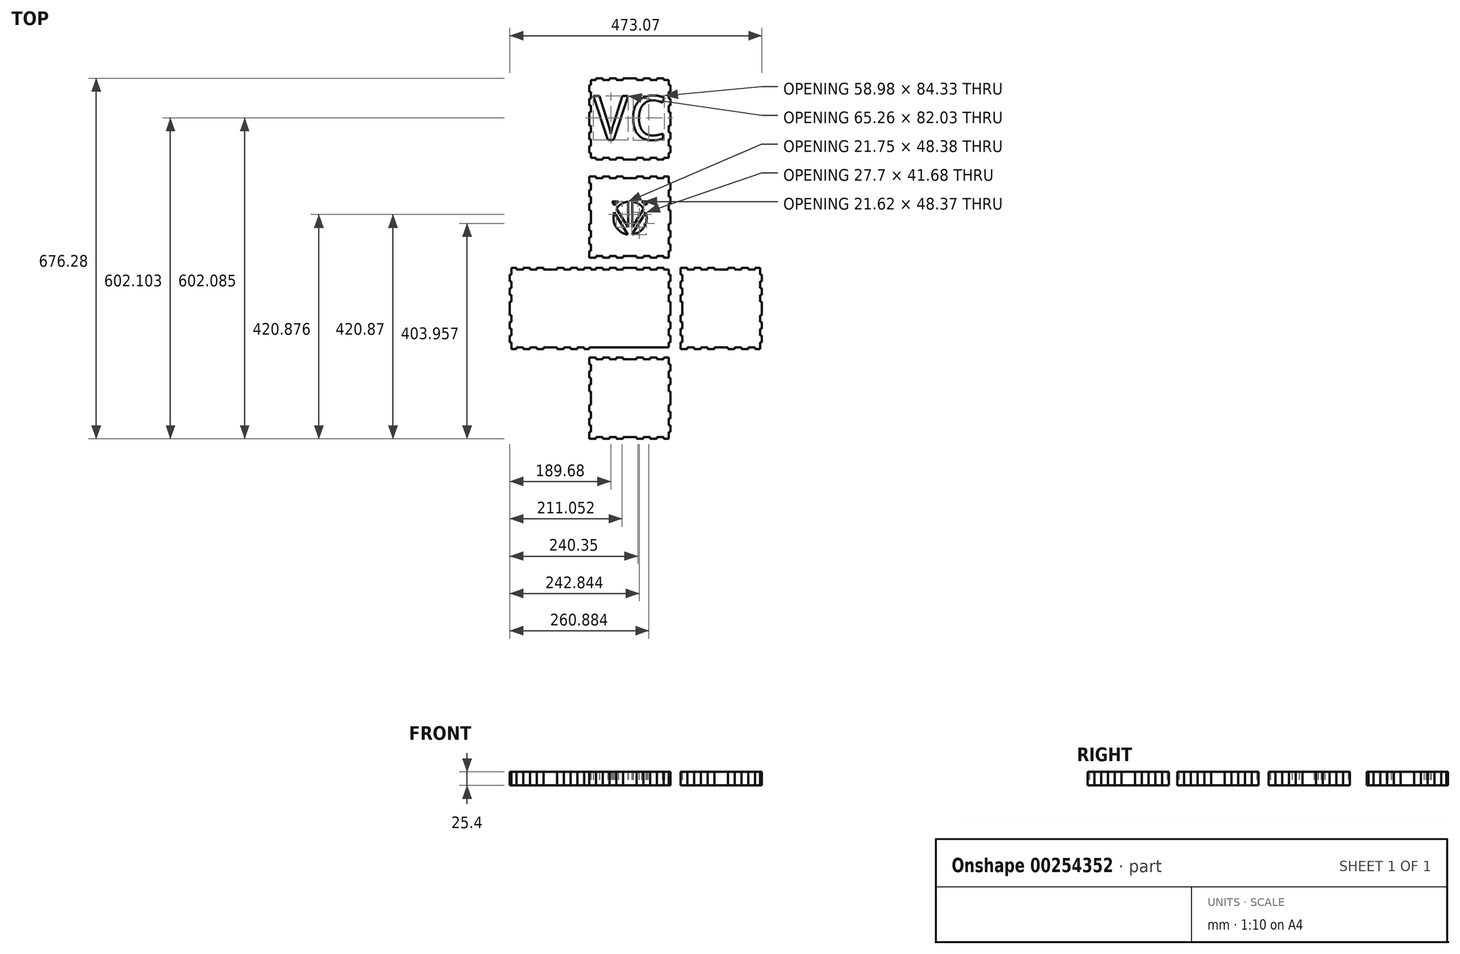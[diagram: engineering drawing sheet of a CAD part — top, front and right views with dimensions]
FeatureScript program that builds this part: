
annotation { "Feature Type Name" : "Feature", "Feature Type Description" : "" }
export const myFeature = defineFeature(function(context is Context, id is Id, definition is map)
    precondition{}
    {
        {
            var Q0;
            Q0=qCreatedBy(makeId("Top.planeOp"),FACE);
            var sketch = newSketch(context, id + "F0", { "sketchPlane" : qUnion([Q0])});
            skLineSegment(sketch, "E0.bottom", {"start": v(-298.45, 152.8) * mm, "end": v(-288.92, 152.8) * mm});
            skLineSegment(sketch, "E0.left", {"start": v(-301.62, 140.1) * mm, "end": v(-301.62, 127.4) * mm});
            skPoint(sketch, "E1", {"position": v(-152.4, 171.86) * mm});
            skLineSegment(sketch, "E2", {"start": v(-149.23, 152.8) * mm, "end": v(-149.23, 140.1) * mm});
            skLineSegment(sketch, "E3", {"start": v(-149.22, 0.4) * mm, "end": v(-161.93, 0.4) * mm});
            skPoint(sketch, "E3.startSnap0", {"position": v(-152.4, -15.47) * mm});
            skLineSegment(sketch, "E4", {"start": v(-152.4, -15.47) * mm, "end": v(-139.7, -15.47) * mm});
            skLineSegment(sketch, "E5", {"start": v(-152.4, -15.47) * mm, "end": v(-152.4, -28.17) * mm});
            skLineSegment(sketch, "E6", {"start": v(-152.4, -167.87) * mm, "end": v(-139.7, -167.87) * mm});
            skLineSegment(sketch, "E7.bottom", {"start": v(-152.4, 171.86) * mm, "end": v(-149.22, 171.86) * mm});
            skLineSegment(sketch, "E7.left", {"start": v(-152.4, 171.86) * mm, "end": v(-152.4, 184.56) * mm});
            skLineSegment(sketch, "E8.top", {"start": v(-139.7, 508.4) * mm, "end": v(-127, 508.4) * mm});
            skLineSegment(sketch, "E9", {"start": v(-149.23, 505.23) * mm, "end": v(-149.23, 359.18) * mm});
            skLineSegment(sketch, "E10", {"start": v(-149.23, 505.23) * mm, "end": v(-76.2, 505.23) * mm});
            skLineSegment(sketch, "E11", {"start": v(-152.4, 321.08) * mm, "end": v(-149.22, 321.08) * mm});
            skLineSegment(sketch, "E12", {"start": v(-152.4, 175.03) * mm, "end": v(-76.2, 175.03) * mm});
            skLineSegment(sketch, "E13", {"start": v(-149.22, 149.63) * mm, "end": v(-225.43, 149.63) * mm});
            skLineSegment(sketch, "E14", {"start": v(-298.45, 152.8) * mm, "end": v(-298.45, 149.63) * mm});
            skLineSegment(sketch, "E15", {"start": v(-152.4, 0.4) * mm, "end": v(-152.4, 25.42) * mm});
            skLineSegment(sketch, "E16", {"start": v(-152.4, -18.64) * mm, "end": v(-149.22, -18.64) * mm});
            skLineSegment(sketch, "E17", {"start": v(-152.4, -164.7) * mm, "end": v(-149.22, -164.7) * mm});
            skLineSegment(sketch, "E18", {"start": v(-149.22, 149.63) * mm, "end": v(-101.6, 149.63) * mm});
            skPoint(sketch, "E19.positionSnap0", {"position": v(-152.4, 432.2) * mm});
            skLineSegment(sketch, "E20", {"start": v(-139.7, 508.4) * mm, "end": v(-139.7, 505.23) * mm});
            skLineSegment(sketch, "E21", {"start": v(-76.2, -164.7) * mm, "end": v(-76.2, -18.64) * mm});
            skLineSegment(sketch, "E22", {"start": v(-127, 508.4) * mm, "end": v(-127, 505.23) * mm});
            skLineSegment(sketch, "E23", {"start": v(-114.3, 508.4) * mm, "end": v(-114.3, 505.23) * mm});
            skLineSegment(sketch, "E24", {"start": v(-101.6, -167.87) * mm, "end": v(-101.6, -164.7) * mm});
            skLineSegment(sketch, "E25", {"start": v(-88.9, 508.4) * mm, "end": v(-88.9, 505.23) * mm});
            skLineSegment(sketch, "E26", {"start": v(-149.22, 0.4) * mm, "end": v(-149.22, 0.4) * mm});
            skLineSegment(sketch, "E27", {"start": v(-127, -15.47) * mm, "end": v(-114.3, -15.47) * mm});
            skLineSegment(sketch, "E28", {"start": v(-101.6, -15.47) * mm, "end": v(-88.9, -15.47) * mm});
            skLineSegment(sketch, "E29", {"start": v(-149.22, 171.86) * mm, "end": v(-139.7, 171.86) * mm});
            skLineSegment(sketch, "E30", {"start": v(-139.7, 152.8) * mm, "end": v(-139.7, 149.63) * mm});
            skLineSegment(sketch, "E31", {"start": v(-127, 152.8) * mm, "end": v(-127, 149.63) * mm});
            skLineSegment(sketch, "E32", {"start": v(-114.3, 152.8) * mm, "end": v(-114.3, 149.63) * mm});
            skLineSegment(sketch, "E33", {"start": v(-101.6, 171.86) * mm, "end": v(-101.6, 175.03) * mm});
            skLineSegment(sketch, "E34", {"start": v(-88.9, 152.8) * mm, "end": v(-88.9, 149.63) * mm});
            skLineSegment(sketch, "E35", {"start": v(-139.7, 324.26) * mm, "end": v(-139.7, 321.08) * mm});
            skLineSegment(sketch, "E36", {"start": v(-127, 324.26) * mm, "end": v(-127, 321.08) * mm});
            skLineSegment(sketch, "E37", {"start": v(-114.3, 324.26) * mm, "end": v(-114.3, 321.08) * mm});
            skLineSegment(sketch, "E38", {"start": v(-101.6, 356) * mm, "end": v(-101.6, 359.18) * mm});
            skLineSegment(sketch, "E39", {"start": v(-88.9, 324.26) * mm, "end": v(-88.9, 321.08) * mm});
            skLineSegment(sketch, "E40", {"start": v(-161.93, 152.8) * mm, "end": v(-161.93, 149.63) * mm});
            skLineSegment(sketch, "E41", {"start": v(-174.62, 0.4) * mm, "end": v(-174.62, 3.58) * mm});
            skLineSegment(sketch, "E42", {"start": v(-187.33, 152.8) * mm, "end": v(-187.33, 149.63) * mm});
            skLineSegment(sketch, "E43", {"start": v(-200.02, 0.4) * mm, "end": v(-200.02, 3.58) * mm});
            skLineSegment(sketch, "E44", {"start": v(-212.73, 152.8) * mm, "end": v(-212.73, 149.63) * mm});
            skLineSegment(sketch, "E45", {"start": v(-238.13, 0.4) * mm, "end": v(-238.13, 3.58) * mm});
            skLineSegment(sketch, "E46", {"start": v(-250.83, 0.4) * mm, "end": v(-250.83, 3.58) * mm});
            skLineSegment(sketch, "E47", {"start": v(-263.52, 0.4) * mm, "end": v(-263.52, 3.58) * mm});
            skLineSegment(sketch, "E48", {"start": v(-276.22, 0.4) * mm, "end": v(-276.22, 3.58) * mm});
            skLineSegment(sketch, "E49", {"start": v(-288.92, 0.4) * mm, "end": v(-288.92, 3.58) * mm});
            skLineSegment(sketch, "E50", {"start": v(-152.4, 495.7) * mm, "end": v(-149.23, 495.7) * mm});
            skLineSegment(sketch, "E51", {"start": v(-152.4, 483) * mm, "end": v(-149.23, 483) * mm});
            skLineSegment(sketch, "E52", {"start": v(-152.4, 470.3) * mm, "end": v(-149.23, 470.3) * mm});
            skLineSegment(sketch, "E53", {"start": v(-152.4, 457.6) * mm, "end": v(-149.23, 457.6) * mm});
            skLineSegment(sketch, "E54", {"start": v(-152.4, 444.9) * mm, "end": v(-149.23, 444.9) * mm});
            skLineSegment(sketch, "E55", {"start": v(-152.4, 311.56) * mm, "end": v(-149.22, 311.56) * mm});
            skLineSegment(sketch, "E56", {"start": v(-152.4, 286.16) * mm, "end": v(-149.22, 286.16) * mm});
            skLineSegment(sketch, "E57", {"start": v(-152.4, 260.76) * mm, "end": v(-149.22, 260.76) * mm});
            skLineSegment(sketch, "E58", {"start": v(-152.4, 235.36) * mm, "end": v(-149.22, 235.36) * mm});
            skLineSegment(sketch, "E59", {"start": v(-152.4, 222.66) * mm, "end": v(-149.22, 222.66) * mm});
            skLineSegment(sketch, "E60", {"start": v(-152.4, 209.96) * mm, "end": v(-149.22, 209.96) * mm});
            skLineSegment(sketch, "E61", {"start": v(-152.4, 197.26) * mm, "end": v(-149.22, 197.26) * mm});
            skLineSegment(sketch, "E62", {"start": v(-301.63, 140.1) * mm, "end": v(-298.45, 140.1) * mm});
            skLineSegment(sketch, "E63", {"start": v(-301.63, 127.4) * mm, "end": v(-298.45, 127.4) * mm});
            skLineSegment(sketch, "E64", {"start": v(-301.63, 114.7) * mm, "end": v(-298.45, 114.7) * mm});
            skLineSegment(sketch, "E65", {"start": v(-301.63, 89.3) * mm, "end": v(-298.45, 89.3) * mm});
            skLineSegment(sketch, "E66", {"start": v(-301.63, 63.9) * mm, "end": v(-298.45, 63.9) * mm});
            skLineSegment(sketch, "E67", {"start": v(-301.62, 38.5) * mm, "end": v(-298.45, 38.5) * mm});
            skLineSegment(sketch, "E68", {"start": v(-301.62, 13.1) * mm, "end": v(-298.45, 13.1) * mm});
            skLineSegment(sketch, "E69", {"start": v(-152.4, -28.17) * mm, "end": v(-149.22, -28.17) * mm});
            skLineSegment(sketch, "E70", {"start": v(-152.4, -53.57) * mm, "end": v(-149.22, -53.57) * mm});
            skLineSegment(sketch, "E71", {"start": v(-152.4, -78.97) * mm, "end": v(-149.22, -78.97) * mm});
            skLineSegment(sketch, "E72", {"start": v(-152.4, -104.37) * mm, "end": v(-149.22, -104.37) * mm});
            skLineSegment(sketch, "E73", {"start": v(-152.4, -129.77) * mm, "end": v(-149.22, -129.77) * mm});
            skLineSegment(sketch, "E74", {"start": v(-152.4, -155.17) * mm, "end": v(-149.22, -155.17) * mm});
            skLineSegment(sketch, "E75", {"start": v(-88.9, -164.7) * mm, "end": v(-76.2, -164.7) * mm});
            skLineSegment(sketch, "E76", {"start": v(-114.3, -164.7) * mm, "end": v(-88.9, -164.7) * mm});
            skLineSegment(sketch, "E77", {"start": v(-127, -164.7) * mm, "end": v(-114.3, -164.7) * mm});
            skLineSegment(sketch, "E78", {"start": v(-139.7, -164.7) * mm, "end": v(-127, -164.7) * mm});
            skLineSegment(sketch, "E79", {"start": v(-149.22, -164.7) * mm, "end": v(-139.7, -164.7) * mm});
            skLineSegment(sketch, "E80", {"start": v(-149.22, -142.47) * mm, "end": v(-149.22, -155.17) * mm});
            skLineSegment(sketch, "E81", {"start": v(-149.22, -117.07) * mm, "end": v(-149.22, -142.47) * mm});
            skLineSegment(sketch, "E82", {"start": v(-149.22, -91.67) * mm, "end": v(-149.22, -117.07) * mm});
            skLineSegment(sketch, "E83", {"start": v(-149.23, -28.17) * mm, "end": v(-149.23, -40.87) * mm});
            skLineSegment(sketch, "E84", {"start": v(-149.23, -40.87) * mm, "end": v(-149.23, -53.57) * mm});
            skLineSegment(sketch, "E85", {"start": v(-149.23, -53.57) * mm, "end": v(-149.23, -66.27) * mm});
            skLineSegment(sketch, "E86", {"start": v(-149.23, -66.27) * mm, "end": v(-149.22, -78.97) * mm});
            skLineSegment(sketch, "E87", {"start": v(-149.22, -78.97) * mm, "end": v(-149.22, -91.67) * mm});
            skLineSegment(sketch, "E88", {"start": v(-149.22, -18.64) * mm, "end": v(-76.2, -18.64) * mm});
            skLineSegment(sketch, "E89", {"start": v(-101.6, -18.64) * mm, "end": v(-101.6, -15.47) * mm});
            skLineSegment(sketch, "E90", {"start": v(-139.7, -164.7) * mm, "end": v(-139.7, -167.87) * mm});
            skLineSegment(sketch, "E91", {"start": v(-127, -164.7) * mm, "end": v(-127, -167.87) * mm});
            skLineSegment(sketch, "E92", {"start": v(-114.3, -164.7) * mm, "end": v(-114.3, -167.87) * mm});
            skLineSegment(sketch, "E93", {"start": v(-88.9, -164.7) * mm, "end": v(-88.9, -167.87) * mm});
            skLineSegment(sketch, "E94", {"start": v(-149.22, -117.07) * mm, "end": v(-152.4, -117.07) * mm});
            skLineSegment(sketch, "E95", {"start": v(-149.22, -142.47) * mm, "end": v(-152.4, -142.47) * mm});
            skLineSegment(sketch, "E96", {"start": v(-149.22, -155.17) * mm, "end": v(-149.22, -167.87) * mm});
            skLineSegment(sketch, "E97", {"start": v(-149.22, -40.87) * mm, "end": v(-152.4, -40.87) * mm});
            skLineSegment(sketch, "E98", {"start": v(-149.22, -66.27) * mm, "end": v(-152.4, -66.27) * mm});
            skLineSegment(sketch, "E99", {"start": v(-88.9, -15.47) * mm, "end": v(-88.9, -18.64) * mm});
            skLineSegment(sketch, "E100", {"start": v(-114.3, -15.47) * mm, "end": v(-114.3, -18.64) * mm});
            skLineSegment(sketch, "E101", {"start": v(-127, -15.47) * mm, "end": v(-127, -18.64) * mm});
            skLineSegment(sketch, "E102", {"start": v(-139.7, -15.47) * mm, "end": v(-139.7, -18.64) * mm});
            skLineSegment(sketch, "E103", {"start": v(-149.23, 25.8) * mm, "end": v(-152.4, 25.8) * mm});
            skLineSegment(sketch, "E104", {"start": v(-149.22, 38.5) * mm, "end": v(-149.22, 3.58) * mm});
            skLineSegment(sketch, "E105", {"start": v(-149.22, 51.2) * mm, "end": v(-149.22, 38.5) * mm});
            skLineSegment(sketch, "E106", {"start": v(-149.22, 76.6) * mm, "end": v(-149.22, 76.6) * mm});
            skLineSegment(sketch, "E107", {"start": v(-149.22, 102) * mm, "end": v(-152.4, 102) * mm});
            skLineSegment(sketch, "E108", {"start": v(-149.22, 149.63) * mm, "end": v(-149.22, 76.6) * mm});
            skLineSegment(sketch, "E109", {"start": v(-101.6, 149.63) * mm, "end": v(-76.2, 149.63) * mm});
            skLineSegment(sketch, "E110", {"start": v(-76.2, 3.58) * mm, "end": v(-149.22, 3.58) * mm});
            skLineSegment(sketch, "E111", {"start": v(-76.2, 3.58) * mm, "end": v(-76.2, 152.8) * mm});
            skLineSegment(sketch, "E112", {"start": v(-101.6, 149.63) * mm, "end": v(-101.6, 152.8) * mm});
            skLineSegment(sketch, "E113", {"start": v(-149.23, 51.2) * mm, "end": v(-152.4, 51.2) * mm});
            skLineSegment(sketch, "E114", {"start": v(-149.22, 76.6) * mm, "end": v(-149.22, 51.2) * mm});
            skLineSegment(sketch, "E115", {"start": v(-149.23, 76.6) * mm, "end": v(-152.4, 76.6) * mm});
            skLineSegment(sketch, "E116", {"start": v(-161.93, 3.58) * mm, "end": v(-161.93, 0.4) * mm});
            skLineSegment(sketch, "E117", {"start": v(-187.32, 3.58) * mm, "end": v(-187.32, 0.4) * mm});
            skLineSegment(sketch, "E118", {"start": v(-212.73, 3.58) * mm, "end": v(-212.73, 0.4) * mm});
            skLineSegment(sketch, "E119", {"start": v(-152.4, 13.1) * mm, "end": v(-149.22, 13.1) * mm});
            skLineSegment(sketch, "E120", {"start": v(-152.4, 25.42) * mm, "end": v(-152.4, 127.4) * mm});
            skLineSegment(sketch, "E121", {"start": v(-152.4, 38.5) * mm, "end": v(-149.22, 38.5) * mm});
            skLineSegment(sketch, "E122", {"start": v(-152.4, 63.9) * mm, "end": v(-149.22, 63.9) * mm});
            skLineSegment(sketch, "E123", {"start": v(-152.4, 89.3) * mm, "end": v(-149.22, 89.3) * mm});
            skLineSegment(sketch, "E124", {"start": v(-152.4, 114.7) * mm, "end": v(-149.22, 114.7) * mm});
            skLineSegment(sketch, "E125", {"start": v(-152.4, 127.4) * mm, "end": v(-152.4, 140.1) * mm});
            skLineSegment(sketch, "E126", {"start": v(-152.4, 127.4) * mm, "end": v(-149.22, 127.4) * mm});
            skLineSegment(sketch, "E127", {"start": v(-152.4, 140.1) * mm, "end": v(-152.4, 152.8) * mm});
            skLineSegment(sketch, "E128", {"start": v(-152.4, 140.1) * mm, "end": v(-149.22, 140.1) * mm});
            skLineSegment(sketch, "E129", {"start": v(-174.63, 149.63) * mm, "end": v(-174.62, 152.8) * mm});
            skLineSegment(sketch, "E130", {"start": v(-200.03, 149.63) * mm, "end": v(-200.03, 152.8) * mm});
            skLineSegment(sketch, "E131", {"start": v(-225.43, 149.63) * mm, "end": v(-263.53, 149.63) * mm});
            skLineSegment(sketch, "E132", {"start": v(-238.13, 149.63) * mm, "end": v(-238.13, 152.8) * mm});
            skLineSegment(sketch, "E133", {"start": v(-250.83, 149.63) * mm, "end": v(-250.83, 152.8) * mm});
            skLineSegment(sketch, "E134", {"start": v(-276.23, 149.63) * mm, "end": v(-276.23, 152.8) * mm});
            skLineSegment(sketch, "E135", {"start": v(-288.92, 149.63) * mm, "end": v(-288.92, 152.8) * mm});
            skLineSegment(sketch, "E136", {"start": v(-298.45, 149.63) * mm, "end": v(-298.45, 0.4) * mm});
            skLineSegment(sketch, "E137", {"start": v(-263.53, 149.63) * mm, "end": v(-298.45, 149.63) * mm});
            skLineSegment(sketch, "E138", {"start": v(-263.53, 149.63) * mm, "end": v(-263.53, 152.8) * mm});
            skLineSegment(sketch, "E139", {"start": v(-298.45, 102) * mm, "end": v(-301.63, 102) * mm});
            skLineSegment(sketch, "E140", {"start": v(-298.45, 76.6) * mm, "end": v(-301.62, 76.6) * mm});
            skLineSegment(sketch, "E141", {"start": v(-298.45, 51.2) * mm, "end": v(-301.62, 51.2) * mm});
            skLineSegment(sketch, "E142", {"start": v(-298.45, 25.8) * mm, "end": v(-301.62, 25.8) * mm});
            skLineSegment(sketch, "E143", {"start": v(-298.45, 3.58) * mm, "end": v(-149.23, 3.58) * mm});
            skLineSegment(sketch, "E144", {"start": v(-88.9, 175.03) * mm, "end": v(-88.9, 171.86) * mm});
            skLineSegment(sketch, "E145", {"start": v(-114.3, 175.03) * mm, "end": v(-114.3, 171.86) * mm});
            skLineSegment(sketch, "E146", {"start": v(-127, 175.03) * mm, "end": v(-127, 171.86) * mm});
            skLineSegment(sketch, "E147", {"start": v(-139.7, 175.03) * mm, "end": v(-139.7, 171.86) * mm});
            skLineSegment(sketch, "E148", {"start": v(-149.22, 175.03) * mm, "end": v(-149.22, 171.86) * mm});
            skLineSegment(sketch, "E149", {"start": v(-149.22, 184.56) * mm, "end": v(-149.22, 175.03) * mm});
            skLineSegment(sketch, "E150", {"start": v(-149.22, 273.46) * mm, "end": v(-152.4, 273.46) * mm});
            skLineSegment(sketch, "E151", {"start": v(-149.22, 298.86) * mm, "end": v(-152.4, 298.86) * mm});
            skLineSegment(sketch, "E152", {"start": v(-149.22, 321.08) * mm, "end": v(-101.6, 321.08) * mm});
            skLineSegment(sketch, "E153", {"start": v(-101.6, 321.08) * mm, "end": v(-76.2, 321.08) * mm});
            skLineSegment(sketch, "E154", {"start": v(-101.6, 321.08) * mm, "end": v(-101.6, 324.26) * mm});
            skLineSegment(sketch, "E155", {"start": v(-149.22, 184.56) * mm, "end": v(-152.4, 184.56) * mm});
            skLineSegment(sketch, "E156", {"start": v(-101.6, 505.23) * mm, "end": v(-101.6, 508.4) * mm});
            skLineSegment(sketch, "E157", {"start": v(-149.23, 432.2) * mm, "end": v(-152.4, 432.2) * mm});
            skLineSegment(sketch, "E158", {"start": v(-149.23, 419.5) * mm, "end": v(-152.4, 419.5) * mm});
            skLineSegment(sketch, "E159", {"start": v(-149.23, 406.8) * mm, "end": v(-152.4, 406.8) * mm});
            skLineSegment(sketch, "E160", {"start": v(-149.23, 394.1) * mm, "end": v(-152.4, 394.1) * mm});
            skLineSegment(sketch, "E161", {"start": v(-149.23, 381.4) * mm, "end": v(-152.4, 381.4) * mm});
            skLineSegment(sketch, "E162", {"start": v(-149.23, 368.7) * mm, "end": v(-152.4, 368.7) * mm});
            skLineSegment(sketch, "E163", {"start": v(-149.23, 359.18) * mm, "end": v(-76.2, 359.18) * mm});
            skLineSegment(sketch, "E164", {"start": v(-139.7, 359.18) * mm, "end": v(-139.7, 356) * mm});
            skLineSegment(sketch, "E165", {"start": v(-127, 359.18) * mm, "end": v(-127, 356) * mm});
            skLineSegment(sketch, "E166", {"start": v(-114.3, 359.18) * mm, "end": v(-114.3, 356) * mm});
            skLineSegment(sketch, "E167", {"start": v(-88.9, 359.18) * mm, "end": v(-88.9, 356) * mm});
            skPoint(sketch, "E168.orphan", {"position": v(-152.4, 508.4) * mm});
            skPoint(sketch, "E169.orphan", {"position": v(-149.23, 508.4) * mm});
            skPoint(sketch, "E170.orphan", {"position": v(-152.4, 505.23) * mm});
            skLineSegment(sketch, "E171.trimOffspring", {"start": v(-114.3, 508.4) * mm, "end": v(-101.6, 508.4) * mm});
            skLineSegment(sketch, "E172.trimOffspring", {"start": v(-88.9, 508.4) * mm, "end": v(-76.2, 508.4) * mm});
            skLineSegment(sketch, "E173.trimOffspring", {"start": v(-152.4, 483) * mm, "end": v(-152.4, 495.7) * mm});
            skLineSegment(sketch, "E174.trimOffspring", {"start": v(-152.4, 457.6) * mm, "end": v(-152.4, 470.3) * mm});
            skLineSegment(sketch, "E175.trimOffspring", {"start": v(-152.4, 419.5) * mm, "end": v(-152.4, 444.9) * mm});
            skLineSegment(sketch, "E176.trimOffspring", {"start": v(-152.4, 394.1) * mm, "end": v(-152.4, 406.8) * mm});
            skLineSegment(sketch, "E177.trimOffspring", {"start": v(-152.4, 368.7) * mm, "end": v(-152.4, 381.4) * mm});
            skLineSegment(sketch, "E178", {"start": v(-149.22, 324.26) * mm, "end": v(-149.22, 184.56) * mm});
            skLineSegment(sketch, "E179", {"start": v(-76.02, 356) * mm, "end": v(-76.02, 508.4) * mm});
            skPoint(sketch, "E8.left.end.orphan", {"position": v(-152.4, 359.18) * mm});
            skLineSegment(sketch, "E180.trimOffspring", {"start": v(-139.7, 356) * mm, "end": v(-127, 356) * mm});
            skPoint(sketch, "E7.top.start.orphan", {"position": v(-152.4, 356) * mm});
            skLineSegment(sketch, "E181.trimOffspring", {"start": v(-114.3, 356) * mm, "end": v(-101.6, 356) * mm});
            skLineSegment(sketch, "E182.trimOffspring", {"start": v(-88.9, 356) * mm, "end": v(-76.2, 356) * mm});
            skLineSegment(sketch, "E183", {"start": v(-88.9, 324.26) * mm, "end": v(-101.6, 324.26) * mm});
            skLineSegment(sketch, "E184", {"start": v(-114.3, 324.26) * mm, "end": v(-127, 324.26) * mm});
            skLineSegment(sketch, "E185", {"start": v(-139.7, 324.26) * mm, "end": v(-149.22, 324.26) * mm});
            skLineSegment(sketch, "E186", {"start": v(-149.22, 324.26) * mm, "end": v(-152.4, 324.26) * mm});
            skLineSegment(sketch, "E187.trimOffspring", {"start": v(-152.4, 311.56) * mm, "end": v(-152.4, 324.26) * mm});
            skLineSegment(sketch, "E188.trimOffspring", {"start": v(-152.4, 286.16) * mm, "end": v(-152.4, 298.86) * mm});
            skLineSegment(sketch, "E189.trimOffspring", {"start": v(-152.4, 260.76) * mm, "end": v(-152.4, 273.46) * mm});
            skLineSegment(sketch, "E190.trimOffspring", {"start": v(-152.4, 197.26) * mm, "end": v(-152.4, 209.96) * mm});
            skLineSegment(sketch, "E191.trimOffspring", {"start": v(-152.4, 222.66) * mm, "end": v(-152.4, 235.36) * mm});
            skPoint(sketch, "E192.end.orphan", {"position": v(-152.4, 248.06) * mm});
            skLineSegment(sketch, "E193.trimOffspring", {"start": v(-127, 171.86) * mm, "end": v(-114.3, 171.86) * mm});
            skLineSegment(sketch, "E194.trimOffspring", {"start": v(-101.6, 171.86) * mm, "end": v(-88.9, 171.86) * mm});
            skLineSegment(sketch, "E195", {"start": v(-139.7, 152.8) * mm, "end": v(-127, 152.8) * mm});
            skLineSegment(sketch, "E196", {"start": v(-149.23, 63.9) * mm, "end": v(-149.23, 51.2) * mm});
            skLineSegment(sketch, "E197", {"start": v(-149.23, 38.5) * mm, "end": v(-149.23, 25.8) * mm});
            skLineSegment(sketch, "E198", {"start": v(-149.23, -15.47) * mm, "end": v(-149.23, -18.64) * mm});
            skLineSegment(sketch, "E199.trimOffspring", {"start": v(-114.3, 152.8) * mm, "end": v(-101.6, 152.8) * mm});
            skLineSegment(sketch, "E200.trimOffspring", {"start": v(-88.9, 152.8) * mm, "end": v(-76.2, 152.8) * mm});
            skLineSegment(sketch, "E201", {"start": v(-152.4, 140.1) * mm, "end": v(-152.4, 127.4) * mm});
            skLineSegment(sketch, "E202", {"start": v(-152.4, 114.7) * mm, "end": v(-152.4, 102) * mm});
            skLineSegment(sketch, "E203", {"start": v(-152.4, 89.3) * mm, "end": v(-152.4, 76.6) * mm});
            skLineSegment(sketch, "E204", {"start": v(-152.4, 76.6) * mm, "end": v(-152.4, 63.9) * mm});
            skLineSegment(sketch, "E205", {"start": v(-152.4, 51.2) * mm, "end": v(-152.4, 38.5) * mm});
            skLineSegment(sketch, "E206", {"start": v(-152.4, 25.8) * mm, "end": v(-152.4, 13.1) * mm});
            skLineSegment(sketch, "E207", {"start": v(-76.2, -18.64) * mm, "end": v(-76.2, -15.47) * mm});
            skLineSegment(sketch, "E208", {"start": v(-149.22, -15.47) * mm, "end": v(-149.23, -28.17) * mm});
            skLineSegment(sketch, "E209", {"start": v(-139.7, -18.64) * mm, "end": v(-127, -18.64) * mm});
            skLineSegment(sketch, "E210", {"start": v(-114.3, -18.64) * mm, "end": v(-101.6, -18.64) * mm});
            skLineSegment(sketch, "E211", {"start": v(-88.9, -18.64) * mm, "end": v(-76.2, -18.64) * mm});
            skLineSegment(sketch, "E212.trimOffspring", {"start": v(-152.4, -40.87) * mm, "end": v(-152.4, -53.57) * mm});
            skLineSegment(sketch, "E213.trimOffspring", {"start": v(-152.4, -66.27) * mm, "end": v(-152.4, -78.97) * mm});
            skLineSegment(sketch, "E214.trimOffspring", {"start": v(-152.4, -155.17) * mm, "end": v(-152.4, -167.87) * mm});
            skLineSegment(sketch, "E215.trimOffspring", {"start": v(-152.4, -129.77) * mm, "end": v(-152.4, -142.47) * mm});
            skLineSegment(sketch, "E216.trimOffspring", {"start": v(-152.4, -104.37) * mm, "end": v(-152.4, -117.07) * mm});
            skPoint(sketch, "E217.end.orphan", {"position": v(-152.4, -91.67) * mm});
            skLineSegment(sketch, "E218.trimOffspring", {"start": v(-127, -167.87) * mm, "end": v(-114.3, -167.87) * mm});
            skLineSegment(sketch, "E219.trimOffspring", {"start": v(-101.6, -167.87) * mm, "end": v(-88.9, -167.87) * mm});
            skLineSegment(sketch, "E220.trimOffspring", {"start": v(-149.23, 127.4) * mm, "end": v(-149.23, 114.7) * mm});
            skLineSegment(sketch, "E221.trimOffspring", {"start": v(-149.23, 102) * mm, "end": v(-149.23, 89.3) * mm});
            skPoint(sketch, "E222.orphan", {"position": v(-149.23, 76.6) * mm});
            skLineSegment(sketch, "E223.trimOffspring", {"start": v(-149.23, -5.94) * mm, "end": v(-149.23, -15.47) * mm});
            skLineSegment(sketch, "E224.trimOffspring", {"start": v(-174.62, 0.4) * mm, "end": v(-187.32, 0.4) * mm});
            skLineSegment(sketch, "E225.trimOffspring", {"start": v(-200.02, 0.4) * mm, "end": v(-212.73, 0.4) * mm});
            skLineSegment(sketch, "E226.trimOffspring", {"start": v(-238.13, 0.4) * mm, "end": v(-250.83, 0.4) * mm});
            skLineSegment(sketch, "E227.trimOffspring", {"start": v(-263.52, 0.4) * mm, "end": v(-276.22, 0.4) * mm});
            skLineSegment(sketch, "E228.trimOffspring", {"start": v(-288.92, 0.4) * mm, "end": v(-298.45, 0.4) * mm});
            skPoint(sketch, "E229.start.orphan", {"position": v(-301.63, 3.58) * mm});
            skLineSegment(sketch, "E230.trimOffspring", {"start": v(-301.62, 25.8) * mm, "end": v(-301.62, 13.1) * mm});
            skLineSegment(sketch, "E231.trimOffspring", {"start": v(-276.23, 152.8) * mm, "end": v(-263.53, 152.8) * mm});
            skLineSegment(sketch, "E232.trimOffspring", {"start": v(-250.83, 152.8) * mm, "end": v(-238.13, 152.8) * mm});
            skPoint(sketch, "E233.orphan", {"position": v(-301.62, 149.63) * mm});
            skLineSegment(sketch, "E234.trimOffspring", {"start": v(-212.73, 152.8) * mm, "end": v(-200.03, 152.8) * mm});
            skLineSegment(sketch, "E235.trimOffspring", {"start": v(-187.33, 152.8) * mm, "end": v(-174.63, 152.8) * mm});
            skPoint(sketch, "E236.end.orphan", {"position": v(-225.43, 152.8) * mm});
            skLineSegment(sketch, "E237.trimOffspring", {"start": v(-161.93, 152.8) * mm, "end": v(-149.23, 152.8) * mm});
            skLineSegment(sketch, "E238.trimOffspring", {"start": v(-301.62, 114.7) * mm, "end": v(-301.62, 102) * mm});
            skLineSegment(sketch, "E239.trimOffspring", {"start": v(-301.62, 89.3) * mm, "end": v(-301.62, 63.9) * mm});
            skLineSegment(sketch, "E240.trimOffspring", {"start": v(-301.62, 51.2) * mm, "end": v(-301.62, 38.5) * mm});
            skLineSegment(sketch, "E241.MirrorCS", {"start": v(44.45, 0.4) * mm, "end": v(57.15, 0.4) * mm});
            skLineSegment(sketch, "E242.MirrorCS", {"start": v(44.45, 0.4) * mm, "end": v(44.45, 3.58) * mm});
            skLineSegment(sketch, "E243.MirrorCS", {"start": v(57.15, 3.58) * mm, "end": v(57.15, 0.4) * mm});
            skLineSegment(sketch, "E244.MirrorCS", {"start": v(31.75, 3.58) * mm, "end": v(31.75, 0.4) * mm});
            skLineSegment(sketch, "E245.MirrorCS", {"start": v(-3.17, 51.2) * mm, "end": v(0, 51.2) * mm});
            skLineSegment(sketch, "E246.MirrorCS", {"start": v(-12.7, 324.26) * mm, "end": v(-12.7, 321.08) * mm});
            skLineSegment(sketch, "E247.MirrorCS", {"start": v(-3.17, -15.47) * mm, "end": v(-3.17, -28.17) * mm});
            skLineSegment(sketch, "E248.MirrorCS", {"start": v(-25.4, 324.26) * mm, "end": v(-25.4, 321.08) * mm});
            skLineSegment(sketch, "E249.MirrorCS", {"start": v(-12.7, -15.47) * mm, "end": v(-12.7, -18.64) * mm});
            skLineSegment(sketch, "E250.MirrorCS", {"start": v(0, 311.56) * mm, "end": v(-3.18, 311.56) * mm});
            skLineSegment(sketch, "E251.MirrorCS", {"start": v(0, -28.17) * mm, "end": v(-3.17, -28.17) * mm});
            skLineSegment(sketch, "E252.MirrorCS", {"start": v(-3.17, -15.47) * mm, "end": v(-12.7, -15.47) * mm});
            skLineSegment(sketch, "E253.MirrorCS", {"start": v(-12.7, 324.26) * mm, "end": v(-3.18, 324.26) * mm});
            skLineSegment(sketch, "E254.MirrorCS", {"start": v(-3.17, -142.47) * mm, "end": v(0, -142.47) * mm});
            skLineSegment(sketch, "E255.MirrorCS", {"start": v(171.45, 38.5) * mm, "end": v(168.28, 38.5) * mm});
            skLineSegment(sketch, "E256.MirrorCS", {"start": v(-50.8, -18.64) * mm, "end": v(-50.8, -15.47) * mm});
            skLineSegment(sketch, "E257.MirrorCS", {"start": v(-3.17, -164.7) * mm, "end": v(-12.7, -164.7) * mm});
            skLineSegment(sketch, "E258.MirrorCS", {"start": v(146.05, 0.4) * mm, "end": v(146.05, 3.58) * mm});
            skLineSegment(sketch, "E259.MirrorCS", {"start": v(-3.17, -66.27) * mm, "end": v(0, -66.27) * mm});
            skLineSegment(sketch, "E260.MirrorCS", {"start": v(-3.17, 76.6) * mm, "end": v(0, 76.6) * mm});
            skLineSegment(sketch, "E261.MirrorCS", {"start": v(168.27, 25.8) * mm, "end": v(171.45, 25.8) * mm});
            skLineSegment(sketch, "E262.MirrorCS", {"start": v(0, 51.2) * mm, "end": v(0, 38.5) * mm});
            skLineSegment(sketch, "E263.MirrorCS", {"start": v(-63.5, 324.26) * mm, "end": v(-50.8, 324.26) * mm});
            skLineSegment(sketch, "E264.MirrorCS", {"start": v(168.27, 51.2) * mm, "end": v(171.45, 51.2) * mm});
            skLineSegment(sketch, "E265.MirrorCS", {"start": v(171.45, 140.1) * mm, "end": v(168.28, 140.1) * mm});
            skLineSegment(sketch, "E266.MirrorCS", {"start": v(0, 13.1) * mm, "end": v(-3.17, 13.1) * mm});
            skLineSegment(sketch, "E267.MirrorCS", {"start": v(171.45, 63.9) * mm, "end": v(168.28, 63.9) * mm});
            skLineSegment(sketch, "E268.MirrorCS", {"start": v(-3.17, -40.87) * mm, "end": v(0, -40.87) * mm});
            skLineSegment(sketch, "E269.MirrorCS", {"start": v(0, 89.3) * mm, "end": v(0, 76.6) * mm});
            skLineSegment(sketch, "E270.MirrorCS", {"start": v(-3.17, 368.7) * mm, "end": v(0, 368.7) * mm});
            skLineSegment(sketch, "E271.MirrorCS", {"start": v(-3.17, 394.1) * mm, "end": v(0, 394.1) * mm});
            skLineSegment(sketch, "E272.MirrorCS", {"start": v(133.35, 0.4) * mm, "end": v(146.05, 0.4) * mm});
            skLineSegment(sketch, "E273.MirrorCS", {"start": v(0, 89.3) * mm, "end": v(-3.17, 89.3) * mm});
            skLineSegment(sketch, "E274.MirrorCS", {"start": v(-38.1, 324.26) * mm, "end": v(-25.4, 324.26) * mm});
            skLineSegment(sketch, "E275.MirrorCS", {"start": v(-25.4, -15.47) * mm, "end": v(-25.4, -18.64) * mm});
            skLineSegment(sketch, "E276.MirrorCS", {"start": v(168.27, 76.6) * mm, "end": v(171.45, 76.6) * mm});
            skLineSegment(sketch, "E277.MirrorCS", {"start": v(0, 286.16) * mm, "end": v(-3.18, 286.16) * mm});
            skLineSegment(sketch, "E278.MirrorCS", {"start": v(0, 38.5) * mm, "end": v(-3.17, 38.5) * mm});
            skLineSegment(sketch, "E279.MirrorCS", {"start": v(171.45, 114.7) * mm, "end": v(171.45, 102) * mm});
            skLineSegment(sketch, "E280.MirrorCS", {"start": v(-3.18, 51.2) * mm, "end": v(-3.18, 38.5) * mm});
            skLineSegment(sketch, "E281.MirrorCS", {"start": v(19.05, 3.58) * mm, "end": v(19.05, 0.4) * mm});
            skLineSegment(sketch, "E282.MirrorCS", {"start": v(168.28, 102) * mm, "end": v(171.45, 102) * mm});
            skLineSegment(sketch, "E283.MirrorCS", {"start": v(19.05, 0.4) * mm, "end": v(31.75, 0.4) * mm});
            skLineSegment(sketch, "E284.MirrorCS", {"start": v(-38.1, -15.47) * mm, "end": v(-38.1, -18.64) * mm});
            skLineSegment(sketch, "E285.MirrorCS", {"start": v(171.45, 127.4) * mm, "end": v(168.28, 127.4) * mm});
            skLineSegment(sketch, "E286.MirrorCS", {"start": v(-25.4, -15.47) * mm, "end": v(-38.1, -15.47) * mm});
            skLineSegment(sketch, "E287.MirrorCS", {"start": v(-3.18, 76.6) * mm, "end": v(-3.18, 51.2) * mm});
            skLineSegment(sketch, "E288.MirrorCS", {"start": v(-63.5, 324.26) * mm, "end": v(-63.5, 321.08) * mm});
            skLineSegment(sketch, "E289.MirrorCS", {"start": v(171.45, 114.7) * mm, "end": v(168.28, 114.7) * mm});
            skLineSegment(sketch, "E290.MirrorCS", {"start": v(-38.1, 324.26) * mm, "end": v(-38.1, 321.08) * mm});
            skLineSegment(sketch, "E291.MirrorCS", {"start": v(-12.7, -164.7) * mm, "end": v(-12.7, -167.87) * mm});
            skLineSegment(sketch, "E292.MirrorCS", {"start": v(133.35, 0.4) * mm, "end": v(133.35, 3.58) * mm});
            skLineSegment(sketch, "E293.MirrorCS", {"start": v(0, 76.6) * mm, "end": v(0, 63.9) * mm});
            skLineSegment(sketch, "E294.MirrorCS", {"start": v(-50.8, 321.08) * mm, "end": v(-50.8, 324.26) * mm});
            skLineSegment(sketch, "E295.MirrorCS", {"start": v(19.05, 13.1) * mm, "end": v(19.05, 3.58) * mm});
            skLineSegment(sketch, "E296.MirrorCS", {"start": v(171.45, 89.3) * mm, "end": v(171.45, 63.9) * mm});
            skLineSegment(sketch, "E297.MirrorCS", {"start": v(0, 63.9) * mm, "end": v(-3.17, 63.9) * mm});
            skLineSegment(sketch, "E298.MirrorCS", {"start": v(22.23, 140.1) * mm, "end": v(19.05, 140.1) * mm});
            skLineSegment(sketch, "E299.MirrorCS", {"start": v(158.75, 149.63) * mm, "end": v(158.75, 152.8) * mm});
            skLineSegment(sketch, "E300.MirrorCS", {"start": v(22.23, 13.1) * mm, "end": v(19.05, 13.1) * mm});
            skLineSegment(sketch, "E301.MirrorCS", {"start": v(171.45, 140.1) * mm, "end": v(171.45, 127.4) * mm});
            skLineSegment(sketch, "E302.MirrorCS", {"start": v(171.45, 51.2) * mm, "end": v(171.45, 38.5) * mm});
            skLineSegment(sketch, "E303.MirrorCS", {"start": v(69.85, 0.4) * mm, "end": v(69.85, 3.58) * mm});
            skLineSegment(sketch, "E304.MirrorCS", {"start": v(171.45, 89.3) * mm, "end": v(168.28, 89.3) * mm});
            skLineSegment(sketch, "E305.MirrorCS", {"start": v(158.75, 0.4) * mm, "end": v(158.75, 3.58) * mm});
            skLineSegment(sketch, "E306.MirrorCS", {"start": v(171.45, 25.8) * mm, "end": v(171.45, 13.1) * mm});
            skLineSegment(sketch, "E307.MirrorCS", {"start": v(-3.18, 298.86) * mm, "end": v(0, 298.86) * mm});
            skLineSegment(sketch, "E308.MirrorCS", {"start": v(-3.17, -28.17) * mm, "end": v(-3.17, -40.87) * mm});
            skLineSegment(sketch, "E309.MirrorCS", {"start": v(0, 140.1) * mm, "end": v(-3.17, 140.1) * mm});
            skLineSegment(sketch, "E310.MirrorCS", {"start": v(-12.7, 356) * mm, "end": v(-25.4, 356) * mm});
            skLineSegment(sketch, "E311.MirrorCS", {"start": v(0, 260.76) * mm, "end": v(-3.18, 260.76) * mm});
            skLineSegment(sketch, "E312.MirrorCS", {"start": v(120.65, 152.8) * mm, "end": v(107.95, 152.8) * mm});
            skLineSegment(sketch, "E313.MirrorCS", {"start": v(-3.17, 381.4) * mm, "end": v(0, 381.4) * mm});
            skLineSegment(sketch, "E314.MirrorCS", {"start": v(0, 483) * mm, "end": v(-3.17, 483) * mm});
            skLineSegment(sketch, "E315.MirrorCS", {"start": v(0, -129.77) * mm, "end": v(-3.17, -129.77) * mm});
            skLineSegment(sketch, "E316.MirrorCS", {"start": v(0, -104.37) * mm, "end": v(-3.17, -104.37) * mm});
            skLineSegment(sketch, "E317.MirrorCS", {"start": v(-3.18, -155.17) * mm, "end": v(-3.18, -167.87) * mm});
            skLineSegment(sketch, "E318.MirrorCS", {"start": v(-25.4, 152.8) * mm, "end": v(-25.4, 149.63) * mm});
            skLineSegment(sketch, "E319.MirrorCS", {"start": v(-38.1, -18.64) * mm, "end": v(-50.8, -18.64) * mm});
            skLineSegment(sketch, "E320.MirrorCS", {"start": v(-38.1, 152.8) * mm, "end": v(-38.1, 149.63) * mm});
            skLineSegment(sketch, "E321.MirrorCS", {"start": v(31.75, 152.8) * mm, "end": v(19.05, 152.8) * mm});
            skLineSegment(sketch, "E322.MirrorCS", {"start": v(-12.7, 359.18) * mm, "end": v(-12.7, 356) * mm});
            skLineSegment(sketch, "E323.MirrorCS", {"start": v(-3.17, 406.8) * mm, "end": v(0, 406.8) * mm});
            skLineSegment(sketch, "E324.MirrorCS", {"start": v(-3.18, 175.03) * mm, "end": v(-3.18, 171.86) * mm});
            skLineSegment(sketch, "E325.MirrorCS", {"start": v(107.95, 149.63) * mm, "end": v(107.95, 152.8) * mm});
            skLineSegment(sketch, "E326.MirrorCS", {"start": v(0, 495.7) * mm, "end": v(-3.17, 495.7) * mm});
            skLineSegment(sketch, "E327.MirrorCS", {"start": v(-25.4, -164.7) * mm, "end": v(-25.4, -167.87) * mm});
            skLineSegment(sketch, "E328.MirrorCS", {"start": v(146.05, 152.8) * mm, "end": v(133.35, 152.8) * mm});
            skLineSegment(sketch, "E329.MirrorCS", {"start": v(22.22, 127.4) * mm, "end": v(22.22, 140.1) * mm});
            skLineSegment(sketch, "E330.MirrorCS", {"start": v(-38.1, 356) * mm, "end": v(-50.8, 356) * mm});
            skLineSegment(sketch, "E331.MirrorCS", {"start": v(-3.17, -40.87) * mm, "end": v(-3.17, -53.57) * mm});
            skLineSegment(sketch, "E332.MirrorCS", {"start": v(0, 127.4) * mm, "end": v(-3.17, 127.4) * mm});
            skLineSegment(sketch, "E333.MirrorCS", {"start": v(171.45, 13.1) * mm, "end": v(168.28, 13.1) * mm});
            skLineSegment(sketch, "E334.MirrorCS", {"start": v(0, 470.3) * mm, "end": v(-3.17, 470.3) * mm});
            skLineSegment(sketch, "E335.MirrorCS", {"start": v(120.65, 149.63) * mm, "end": v(120.65, 152.8) * mm});
            skLineSegment(sketch, "E336.MirrorCS", {"start": v(-3.18, 38.5) * mm, "end": v(-3.18, 3.58) * mm});
            skLineSegment(sketch, "E337.MirrorCS", {"start": v(22.23, 38.5) * mm, "end": v(19.05, 38.5) * mm});
            skLineSegment(sketch, "E338.MirrorCS", {"start": v(-3.17, -117.07) * mm, "end": v(0, -117.07) * mm});
            skLineSegment(sketch, "E339.MirrorCS", {"start": v(0, 25.8) * mm, "end": v(0, 13.1) * mm});
            skLineSegment(sketch, "E340.MirrorCS", {"start": v(-63.5, -18.64) * mm, "end": v(-76.2, -18.64) * mm});
            skLineSegment(sketch, "E341.MirrorCS", {"start": v(31.75, 152.8) * mm, "end": v(31.75, 149.63) * mm});
            skLineSegment(sketch, "E342.MirrorCS", {"start": v(-25.4, 359.18) * mm, "end": v(-25.4, 356) * mm});
            skLineSegment(sketch, "E343.MirrorCS", {"start": v(-38.1, -164.7) * mm, "end": v(-38.1, -167.87) * mm});
            skLineSegment(sketch, "E344.MirrorCS", {"start": v(-12.7, -164.7) * mm, "end": v(-25.4, -164.7) * mm});
            skLineSegment(sketch, "E345.MirrorCS", {"start": v(133.35, 149.63) * mm, "end": v(168.28, 149.63) * mm});
            skLineSegment(sketch, "E346.MirrorCS", {"start": v(0, 394.1) * mm, "end": v(0, 406.8) * mm});
            skLineSegment(sketch, "E347.MirrorCS", {"start": v(19.05, 25.8) * mm, "end": v(22.23, 25.8) * mm});
            skLineSegment(sketch, "E348.MirrorCS", {"start": v(69.85, 0.4) * mm, "end": v(82.55, 0.4) * mm});
            skLineSegment(sketch, "E349.MirrorCS", {"start": v(-25.4, 508.4) * mm, "end": v(-25.4, 505.23) * mm});
            skLineSegment(sketch, "E350.MirrorCS", {"start": v(-3.17, -78.97) * mm, "end": v(-3.18, -91.67) * mm});
            skLineSegment(sketch, "E351.MirrorCS", {"start": v(0, -78.97) * mm, "end": v(-3.17, -78.97) * mm});
            skLineSegment(sketch, "E352.MirrorCS", {"start": v(-12.7, -18.64) * mm, "end": v(-25.4, -18.64) * mm});
            skLineSegment(sketch, "E353.MirrorCS", {"start": v(0, -155.17) * mm, "end": v(-3.17, -155.17) * mm});
            skLineSegment(sketch, "E354.MirrorCS", {"start": v(-3.17, -167.87) * mm, "end": v(-12.7, -167.87) * mm});
            skLineSegment(sketch, "E355.MirrorCS", {"start": v(19.05, 38.5) * mm, "end": v(19.05, 25.8) * mm});
            skLineSegment(sketch, "E356.MirrorCS", {"start": v(168.28, 152.8) * mm, "end": v(168.28, 149.63) * mm});
            skLineSegment(sketch, "E357.MirrorCS", {"start": v(-3.18, 321.08) * mm, "end": v(-50.8, 321.08) * mm});
            skLineSegment(sketch, "E358.MirrorCS", {"start": v(-3.17, -53.57) * mm, "end": v(-3.17, -66.27) * mm});
            skLineSegment(sketch, "E359.MirrorCS", {"start": v(120.65, 0.4) * mm, "end": v(120.65, 3.58) * mm});
            skLineSegment(sketch, "E360.MirrorCS", {"start": v(22.23, 127.4) * mm, "end": v(19.05, 127.4) * mm});
            skLineSegment(sketch, "E361.MirrorCS", {"start": v(-3.18, 184.56) * mm, "end": v(0, 184.56) * mm});
            skLineSegment(sketch, "E362.MirrorCS", {"start": v(0, 457.6) * mm, "end": v(-3.17, 457.6) * mm});
            skLineSegment(sketch, "E363.MirrorCS", {"start": v(-3.18, 273.46) * mm, "end": v(0, 273.46) * mm});
            skLineSegment(sketch, "E364.MirrorCS", {"start": v(146.05, 149.63) * mm, "end": v(146.05, 152.8) * mm});
            skLineSegment(sketch, "E365.MirrorCS", {"start": v(0, 114.7) * mm, "end": v(-3.17, 114.7) * mm});
            skLineSegment(sketch, "E366.MirrorCS", {"start": v(82.55, 3.58) * mm, "end": v(82.55, 0.4) * mm});
            skLineSegment(sketch, "E367.MirrorCS", {"start": v(22.22, 0.4) * mm, "end": v(22.22, 25.42) * mm});
            skLineSegment(sketch, "E368.MirrorCS", {"start": v(133.35, 149.63) * mm, "end": v(133.35, 152.8) * mm});
            skLineSegment(sketch, "E369.MirrorCS", {"start": v(0, 368.7) * mm, "end": v(0, 381.4) * mm});
            skLineSegment(sketch, "E370.MirrorCS", {"start": v(-76.2, 0.4) * mm, "end": v(-76.2, 3.58) * mm});
            skLineSegment(sketch, "E371.MirrorCS", {"start": v(168.28, 149.63) * mm, "end": v(168.28, 0.4) * mm});
            skLineSegment(sketch, "E372.MirrorCS", {"start": v(-38.1, 359.18) * mm, "end": v(-38.1, 356) * mm});
            skLineSegment(sketch, "E373.MirrorCS", {"start": v(19.05, 127.4) * mm, "end": v(19.05, 114.7) * mm});
            skLineSegment(sketch, "E374.MirrorCS", {"start": v(168.28, 152.8) * mm, "end": v(158.75, 152.8) * mm});
            skLineSegment(sketch, "E375.MirrorCS", {"start": v(-12.7, 152.8) * mm, "end": v(-12.7, 149.63) * mm});
            skLineSegment(sketch, "E376.MirrorCS", {"start": v(158.75, 0.4) * mm, "end": v(168.28, 0.4) * mm});
            skLineSegment(sketch, "E377.MirrorCS", {"start": v(-63.5, -15.47) * mm, "end": v(-63.5, -18.64) * mm});
            skLineSegment(sketch, "E378.MirrorCS", {"start": v(-3.17, -66.27) * mm, "end": v(-3.17, -78.97) * mm});
            skLineSegment(sketch, "E379.MirrorCS", {"start": v(-3.17, 25.8) * mm, "end": v(0, 25.8) * mm});
            skLineSegment(sketch, "E380.MirrorCS", {"start": v(0, 140.1) * mm, "end": v(0, 127.4) * mm});
            skLineSegment(sketch, "E381.MirrorCS", {"start": v(0, -53.57) * mm, "end": v(-3.17, -53.57) * mm});
            skLineSegment(sketch, "E382.MirrorCS", {"start": v(19.05, 51.2) * mm, "end": v(22.23, 51.2) * mm});
            skLineSegment(sketch, "E383.MirrorCS", {"start": v(-3.18, -142.47) * mm, "end": v(-3.18, -155.17) * mm});
            skLineSegment(sketch, "E384.MirrorCS", {"start": v(19.05, 152.8) * mm, "end": v(19.05, 140.1) * mm});
            skLineSegment(sketch, "E385.MirrorCS", {"start": v(0, 444.9) * mm, "end": v(-3.17, 444.9) * mm});
            skLineSegment(sketch, "E386.MirrorCS", {"start": v(19.05, 102) * mm, "end": v(22.23, 102) * mm});
            skLineSegment(sketch, "E387.MirrorCS", {"start": v(22.22, 140.1) * mm, "end": v(22.22, 152.8) * mm});
            skLineSegment(sketch, "E388.MirrorCS", {"start": v(-25.4, 171.86) * mm, "end": v(-38.1, 171.86) * mm});
            skLineSegment(sketch, "E389.MirrorCS", {"start": v(0, 483) * mm, "end": v(0, 495.7) * mm});
            skLineSegment(sketch, "E390.MirrorCS", {"start": v(-50.8, -167.87) * mm, "end": v(-50.8, -164.7) * mm});
            skLineSegment(sketch, "E391.MirrorCS", {"start": v(-50.8, -15.47) * mm, "end": v(-63.5, -15.47) * mm});
            skLineSegment(sketch, "E392.MirrorCS", {"start": v(-38.1, 152.8) * mm, "end": v(-50.8, 152.8) * mm});
            skLineSegment(sketch, "E393.MirrorCS", {"start": v(-25.4, -164.7) * mm, "end": v(-38.1, -164.7) * mm});
            skLineSegment(sketch, "E394.MirrorCS", {"start": v(-3.17, 419.5) * mm, "end": v(0, 419.5) * mm});
            skLineSegment(sketch, "E395.MirrorCS", {"start": v(0, 114.7) * mm, "end": v(0, 102) * mm});
            skLineSegment(sketch, "E396.MirrorCS", {"start": v(44.45, 149.63) * mm, "end": v(44.45, 152.8) * mm});
            skLineSegment(sketch, "E397.MirrorCS", {"start": v(-3.17, 432.2) * mm, "end": v(0, 432.2) * mm});
            skLineSegment(sketch, "E398.MirrorCS", {"start": v(0, 209.96) * mm, "end": v(-3.18, 209.96) * mm});
            skLineSegment(sketch, "E399.MirrorCS", {"start": v(0, 197.26) * mm, "end": v(-3.18, 197.26) * mm});
            skLineSegment(sketch, "E400.MirrorCS", {"start": v(-12.7, 152.8) * mm, "end": v(-25.4, 152.8) * mm});
            skLineSegment(sketch, "E401.MirrorCS", {"start": v(0, 222.66) * mm, "end": v(-3.18, 222.66) * mm});
            skLineSegment(sketch, "E402.MirrorCS", {"start": v(-12.7, 175.03) * mm, "end": v(-12.7, 171.86) * mm});
            skLineSegment(sketch, "E403.MirrorCS", {"start": v(95.25, 149.63) * mm, "end": v(133.35, 149.63) * mm});
            skLineSegment(sketch, "E404.MirrorCS", {"start": v(-63.5, 152.8) * mm, "end": v(-63.5, 149.63) * mm});
            skLineSegment(sketch, "E405.MirrorCS", {"start": v(-3.17, 149.63) * mm, "end": v(-50.8, 149.63) * mm});
            skLineSegment(sketch, "E406.MirrorCS", {"start": v(69.85, 149.63) * mm, "end": v(69.85, 152.8) * mm});
            skLineSegment(sketch, "E407.MirrorCS", {"start": v(-3.18, 184.56) * mm, "end": v(-3.18, 175.03) * mm});
            skLineSegment(sketch, "E408.MirrorCS", {"start": v(82.55, 152.8) * mm, "end": v(69.85, 152.8) * mm});
            skLineSegment(sketch, "E409.MirrorCS", {"start": v(-3.17, 171.86) * mm, "end": v(-12.7, 171.86) * mm});
            skLineSegment(sketch, "E410.MirrorCS", {"start": v(107.95, 0.4) * mm, "end": v(120.65, 0.4) * mm});
            skLineSegment(sketch, "E411.MirrorCS", {"start": v(107.95, 0.4) * mm, "end": v(107.95, 3.58) * mm});
            skLineSegment(sketch, "E412.MirrorCS", {"start": v(-3.18, -91.67) * mm, "end": v(-3.18, -117.07) * mm});
            skLineSegment(sketch, "E413.MirrorCS", {"start": v(-25.4, -167.87) * mm, "end": v(-38.1, -167.87) * mm});
            skLineSegment(sketch, "E414.MirrorCS", {"start": v(-12.7, 508.4) * mm, "end": v(-25.4, 508.4) * mm});
            skLineSegment(sketch, "E415.MirrorCS", {"start": v(82.55, 152.8) * mm, "end": v(82.55, 149.63) * mm});
            skLineSegment(sketch, "E416.MirrorCS", {"start": v(0, 419.5) * mm, "end": v(0, 444.9) * mm});
            skLineSegment(sketch, "E417.MirrorCS", {"start": v(-63.5, -164.7) * mm, "end": v(-63.5, -167.87) * mm});
            skLineSegment(sketch, "E418.MirrorCS", {"start": v(22.23, 114.7) * mm, "end": v(19.05, 114.7) * mm});
            skLineSegment(sketch, "E419.MirrorCS", {"start": v(-3.17, 359.18) * mm, "end": v(-76.2, 359.18) * mm});
            skLineSegment(sketch, "E420.MirrorCS", {"start": v(57.15, 152.8) * mm, "end": v(44.45, 152.8) * mm});
            skLineSegment(sketch, "E421.MirrorCS", {"start": v(-63.5, 356) * mm, "end": v(-76.2, 356) * mm});
            skLineSegment(sketch, "E422.MirrorCS", {"start": v(-12.7, 508.4) * mm, "end": v(-12.7, 505.23) * mm});
            skLineSegment(sketch, "E423.MirrorCS", {"start": v(0, 457.6) * mm, "end": v(0, 470.3) * mm});
            skLineSegment(sketch, "E424.MirrorCS", {"start": v(19.05, 63.9) * mm, "end": v(19.05, 51.2) * mm});
            skLineSegment(sketch, "E425.MirrorCS", {"start": v(-50.8, -167.87) * mm, "end": v(-63.5, -167.87) * mm});
            skLineSegment(sketch, "E426.MirrorCS", {"start": v(-76.2, 3.58) * mm, "end": v(-3.17, 3.58) * mm});
            skLineSegment(sketch, "E427.MirrorCS", {"start": v(-3.17, 102) * mm, "end": v(0, 102) * mm});
            skLineSegment(sketch, "E428.MirrorCS", {"start": v(-3.18, -117.07) * mm, "end": v(-3.18, -142.47) * mm});
            skLineSegment(sketch, "E429.MirrorCS", {"start": v(-38.1, -164.7) * mm, "end": v(-63.5, -164.7) * mm});
            skLineSegment(sketch, "E430.MirrorCS", {"start": v(-63.5, 359.18) * mm, "end": v(-63.5, 356) * mm});
            skLineSegment(sketch, "E431.MirrorCS", {"start": v(57.15, 152.8) * mm, "end": v(57.15, 149.63) * mm});
            skLineSegment(sketch, "E432.MirrorCS", {"start": v(19.05, 102) * mm, "end": v(19.05, 89.3) * mm});
            skLineSegment(sketch, "E433.MirrorCS", {"start": v(-50.8, 149.63) * mm, "end": v(-50.8, 152.8) * mm});
            skLineSegment(sketch, "E434.MirrorCS", {"start": v(-50.8, 171.86) * mm, "end": v(-63.5, 171.86) * mm});
            skLineSegment(sketch, "E435.MirrorCS", {"start": v(22.23, 89.3) * mm, "end": v(19.05, 89.3) * mm});
            skLineSegment(sketch, "E436.MirrorCS", {"start": v(-3.17, 505.23) * mm, "end": v(-3.17, 359.18) * mm});
            skLineSegment(sketch, "E437.MirrorCS", {"start": v(-50.8, 356) * mm, "end": v(-50.8, 359.18) * mm});
            skLineSegment(sketch, "E438.MirrorCS", {"start": v(22.23, 63.9) * mm, "end": v(19.05, 63.9) * mm});
            skLineSegment(sketch, "E439.MirrorCS", {"start": v(168.28, 3.58) * mm, "end": v(19.05, 3.58) * mm});
            skLineSegment(sketch, "E440.MirrorCS", {"start": v(-38.1, 175.03) * mm, "end": v(-38.1, 171.86) * mm});
            skLineSegment(sketch, "E441.MirrorCS", {"start": v(19.05, 149.63) * mm, "end": v(95.25, 149.63) * mm});
            skLineSegment(sketch, "E442.MirrorCS", {"start": v(-25.4, 175.03) * mm, "end": v(-25.4, 171.86) * mm});
            skLineSegment(sketch, "E443.MirrorCS", {"start": v(-50.8, 321.08) * mm, "end": v(-76.2, 321.08) * mm});
            skLineSegment(sketch, "E444.MirrorCS", {"start": v(-63.5, 175.03) * mm, "end": v(-63.5, 171.86) * mm});
            skLineSegment(sketch, "E445.MirrorCS", {"start": v(-3.17, -18.64) * mm, "end": v(-76.2, -18.64) * mm});
            skLineSegment(sketch, "E446.MirrorCS", {"start": v(-38.1, 508.4) * mm, "end": v(-38.1, 505.23) * mm});
            skLineSegment(sketch, "E447.MirrorCS", {"start": v(-3.18, 175.03) * mm, "end": v(-76.2, 175.03) * mm});
            skLineSegment(sketch, "E448.MirrorCS", {"start": v(-63.5, 152.8) * mm, "end": v(-76.2, 152.8) * mm});
            skLineSegment(sketch, "E449.MirrorCS", {"start": v(-50.8, 149.63) * mm, "end": v(-76.2, 149.63) * mm});
            skLineSegment(sketch, "E450.MirrorCS", {"start": v(-63.5, 508.4) * mm, "end": v(-63.5, 505.23) * mm});
            skLineSegment(sketch, "E451.MirrorCS", {"start": v(-63.5, -164.7) * mm, "end": v(-76.2, -164.7) * mm});
            skLineSegment(sketch, "E452.MirrorCS", {"start": v(-3.18, 149.63) * mm, "end": v(-3.18, 76.6) * mm});
            skLineSegment(sketch, "E453.MirrorCS", {"start": v(0, 235.36) * mm, "end": v(-3.18, 235.36) * mm});
            skLineSegment(sketch, "E454.MirrorCS", {"start": v(-38.1, 508.4) * mm, "end": v(-50.8, 508.4) * mm});
            skLineSegment(sketch, "E455.MirrorCS", {"start": v(22.22, 25.42) * mm, "end": v(22.22, 127.4) * mm});
            skLineSegment(sketch, "E456.MirrorCS", {"start": v(-50.8, 505.23) * mm, "end": v(-50.8, 508.4) * mm});
            skLineSegment(sketch, "E457.MirrorCS", {"start": v(-3.18, 324.26) * mm, "end": v(-3.18, 184.56) * mm});
            skLineSegment(sketch, "E458.MirrorCS", {"start": v(-50.8, 171.86) * mm, "end": v(-50.8, 175.03) * mm});
            skLineSegment(sketch, "E459.MirrorCS", {"start": v(-63.5, 508.4) * mm, "end": v(-76.2, 508.4) * mm});
            skLineSegment(sketch, "E460.MirrorCS", {"start": v(-3.17, 505.23) * mm, "end": v(-76.2, 505.23) * mm});
            skPoint(sketch, "E461.MirrorP", {"position": v(0, 508.4) * mm});
            skPoint(sketch, "E462.MirrorP", {"position": v(0, 359.18) * mm});
            skPoint(sketch, "E463.MirrorP", {"position": v(0, -15.47) * mm});
            skLineSegment(sketch, "E464.MirrorCS", {"start": v(-3.18, 76.6) * mm, "end": v(-3.18, 76.6) * mm});
            skPoint(sketch, "E465.MirrorP", {"position": v(171.45, 149.63) * mm});
            skPoint(sketch, "E466.MirrorP", {"position": v(0, 505.23) * mm});
            skLineSegment(sketch, "E467.MirrorCS", {"start": v(-3.18, 0.4) * mm, "end": v(-3.18, 0.4) * mm});
            skPoint(sketch, "E468.MirrorP", {"position": v(0, 356) * mm});
            skPoint(sketch, "E469.MirrorP", {"position": v(171.45, 3.58) * mm});
            skPoint(sketch, "E470.MirrorP", {"position": v(0, 432.2) * mm});
            skPoint(sketch, "E471.MirrorP", {"position": v(0, 171.86) * mm});
            skPoint(sketch, "E472.MirrorP", {"position": v(0, 248.06) * mm});
            skPoint(sketch, "E473.MirrorP", {"position": v(95.25, 152.8) * mm});
            skPoint(sketch, "E474.MirrorP", {"position": v(0, -91.67) * mm});
            skPoint(sketch, "E475.MirrorP", {"position": v(19.05, 76.6) * mm});
            skPoint(sketch, "E476.MirrorP", {"position": v(-3.17, 508.4) * mm});
            skPoint(sketch, "E477.orphan", {"position": v(0, 324.26) * mm});
            skPoint(sketch, "E478.MirrorCS.start.orphan", {"position": v(0, 321.08) * mm});
            skPoint(sketch, "E479.MirrorCS.end.orphan", {"position": v(0, 175.03) * mm});
            skLineSegment(sketch, "E480", {"start": v(0, 184.56) * mm, "end": v(0, 197.26) * mm});
            skLineSegment(sketch, "E481", {"start": v(0, 209.96) * mm, "end": v(0, 222.66) * mm});
            skLineSegment(sketch, "E482", {"start": v(0, 235.36) * mm, "end": v(0, 260.76) * mm});
            skLineSegment(sketch, "E483", {"start": v(0, 273.46) * mm, "end": v(0, 286.16) * mm});
            skLineSegment(sketch, "E484", {"start": v(0, 298.86) * mm, "end": v(0, 311.56) * mm});
            skPoint(sketch, "E485.MirrorCS.start.orphan", {"position": v(0, -18.64) * mm});
            skPoint(sketch, "E486.MirrorCS.end.orphan", {"position": v(0, -167.87) * mm});
            skPoint(sketch, "E487.MirrorCS.start.orphan", {"position": v(0, -164.7) * mm});
            skLineSegment(sketch, "E488", {"start": v(0, -155.17) * mm, "end": v(0, -142.47) * mm});
            skLineSegment(sketch, "E489", {"start": v(0, -129.77) * mm, "end": v(0, -117.07) * mm});
            skLineSegment(sketch, "E490", {"start": v(0, -104.37) * mm, "end": v(0, -91.67) * mm});
            skLineSegment(sketch, "E491", {"start": v(0, -78.97) * mm, "end": v(0, -91.67) * mm});
            skLineSegment(sketch, "E492", {"start": v(0, -66.27) * mm, "end": v(0, -53.57) * mm});
            skLineSegment(sketch, "E493", {"start": v(0, -40.87) * mm, "end": v(0, -28.17) * mm});
            skText(sketch, "E494", { "text": "VC", "fontName": "DroidSansMono.ttf"});
            skPoint(sketch, "E495.trimOffspring.end.orphan", {"position": v(-76.38, 508.4) * mm});
            skPoint(sketch, "E496.MirrorCS.start.orphan", {"position": v(-76.38, 356) * mm});
            skLineSegment(sketch, "E497", {"start": v(-79.7, 277.2) * mm, "end": v(-79.7, 228.82) * mm});
            skLineSegment(sketch, "E498", {"start": v(-109.45, 277.2) * mm, "end": v(-97.7, 277.2) * mm});
            skLineSegment(sketch, "E499", {"start": v(-109.45, 277.2) * mm, "end": v(-105.18, 270.26) * mm});
            skLineSegment(sketch, "E500", {"start": v(-72.08, 277.2) * mm, "end": v(-72.08, 228.82) * mm});
            skLineSegment(sketch, "E501", {"start": v(-42.54, 277.2) * mm, "end": v(-46.74, 270.32) * mm});
            skLineSegment(sketch, "E502.trimOffspring", {"start": v(-72.18, 277.2) * mm, "end": v(-72.08, 277.2) * mm});
            skArc(sketch, "E503", {"start": v(-105.3, 256.73) * mm, "mid": v(-102.48, 229.9) * mm, "end": v(-79.77, 215.3) * mm});
            skLineSegment(sketch, "E504.trimOffspring", {"start": v(-101.44, 264.18) * mm, "end": v(-79.7, 228.82) * mm});
            skLineSegment(sketch, "E505.trimOffspring", {"start": v(-105.3, 256.73) * mm, "end": v(-79.77, 215.3) * mm});
            skArc(sketch, "E506.trimOffspring", {"start": v(-79.7, 277.2) * mm, "mid": v(-91.95, 273) * mm, "end": v(-101.44, 264.18) * mm});
            skLineSegment(sketch, "E507.trimOffspring", {"start": v(-54.17, 277.2) * mm, "end": v(-42.54, 277.2) * mm});
            skLineSegment(sketch, "E508.trimOffspring", {"start": v(-50.46, 264.22) * mm, "end": v(-72.08, 228.82) * mm});
            skArc(sketch, "E509.trimOffspring", {"start": v(-46.74, 270.32) * mm, "mid": v(-50.22, 274) * mm, "end": v(-54.17, 277.2) * mm});
            skArc(sketch, "E510.trimOffspring", {"start": v(-50.46, 264.22) * mm, "mid": v(-59.94, 273.01) * mm, "end": v(-72.18, 277.2) * mm});
            skLineSegment(sketch, "E511.trimOffspring", {"start": v(-46.65, 256.93) * mm, "end": v(-72.62, 215.25) * mm});
            skLineSegment(sketch, "E512.trimOffspring", {"start": v(-76.2, 284.08) * mm, "end": v(-76.2, 284.24) * mm});
            skArc(sketch, "E513.trimOffspring", {"start": v(-72.62, 215.25) * mm, "mid": v(-49.48, 229.76) * mm, "end": v(-46.65, 256.93) * mm});
            skArc(sketch, "E514.trimOffspring", {"start": v(-97.7, 277.2) * mm, "mid": v(-101.68, 273.98) * mm, "end": v(-105.18, 270.26) * mm});
            skPoint(sketch, "E515.orphan", {"position": v(-76.2, 321.08) * mm});
            const initialGuessF0  = {"E494": [-0.14642, 0.3932, 1, 0, 0.08273]};
            skSetInitialGuess(sketch, initialGuessF0);
            skSolve(sketch);
        }
        {
            var Q0;
            Q0=makeQuery(id+"F0.imprint","IMPRINT",FACE,{"disambiguationData":[TD([[makeQuery(id+"F0.imprint","IMPRINT",EDGE,{"derivedFrom":sQuery(id+"F0.wireOp",EDGE,"E494.sketch_text.stroke-9")}),1.0]])]});
            var Q1;
            {var subQ37=sQuery(id+"F0.wireOp",EDGE,"E125");Q1=makeQuery(id+"F0.imprint","IMPRINT",FACE,{"disambiguationData":[TD([[makeQuery(id+"F0.imprint","IMPRINT",EDGE,{"derivedFrom":subQ37}),1.0]])]});}
            var Q2;
            {var subQ37=sQuery(id+"F0.wireOp",EDGE,"E329.MirrorCS");Q2=makeQuery(id+"F0.imprint","IMPRINT",FACE,{"disambiguationData":[TD([[makeQuery(id+"F0.imprint","IMPRINT",EDGE,{"derivedFrom":subQ37}),-1.0]])]});}
            var Q3;
            {var subQ5=sQuery(id+"F0.wireOp",EDGE,"E149");Q3=makeQuery(id+"F0.imprint","IMPRINT",FACE,{"disambiguationData":[TD([[makeQuery(id+"F0.imprint","IMPRINT",EDGE,{"derivedFrom":subQ5}),1.0]])]});}
            var Q4;
            Q4=makeQuery(id+"F0.imprint","IMPRINT",FACE,{"disambiguationData":[TD([[makeQuery(id+"F0.imprint","IMPRINT",EDGE,{"derivedFrom":sQuery(id+"F0.wireOp",EDGE,"E494.sketch_text.stroke-0")}),1.0]])]});
            var Q5;
            {var subQ25=sQuery(id+"F0.wireOp",EDGE,"E105");Q5=makeQuery(id+"F0.imprint","IMPRINT",FACE,{"disambiguationData":[TD([[makeQuery(id+"F0.imprint","IMPRINT",EDGE,{"derivedFrom":subQ25}),1.0]])]});}
            var Q6;
            {var subQ24=sQuery(id+"F0.wireOp",EDGE,"E280.MirrorCS");Q6=makeQuery(id+"F0.imprint","IMPRINT",FACE,{"disambiguationData":[TD([[makeQuery(id+"F0.imprint","IMPRINT",EDGE,{"derivedFrom":subQ24}),-1.0]])]});}
            var Q7;
            Q7 = qSketchRegion(id + "F0", true);
            var Q8;
            {var subQ20=sQuery(id+"F0.wireOp",EDGE,"E257.MirrorCS");Q8=makeQuery(id+"F0.imprint","IMPRINT",FACE,{"disambiguationData":[TD([[makeQuery(id+"F0.imprint","IMPRINT",EDGE,{"derivedFrom":subQ20}),-1.0]])]});}
            var Q9;
            {var subQ13=sQuery(id+"F0.wireOp",EDGE,"E75");Q9=makeQuery(id+"F0.imprint","IMPRINT",FACE,{"disambiguationData":[TD([[makeQuery(id+"F0.imprint","IMPRINT",EDGE,{"derivedFrom":subQ13}),1.0]])]});}
            var Q10;
            {var subQ0=sQuery(id+"F0.wireOp",EDGE,"E65");Q10=makeQuery(id+"F0.imprint","IMPRINT",FACE,{"disambiguationData":[TD([[makeQuery(id+"F0.imprint","IMPRINT",EDGE,{"derivedFrom":subQ0}),-1.0]])]});}
            var Q11;
            {var subQ0=sQuery(id+"F0.wireOp",EDGE,"E255.MirrorCS");Q11=makeQuery(id+"F0.imprint","IMPRINT",FACE,{"disambiguationData":[TD([[makeQuery(id+"F0.imprint","IMPRINT",EDGE,{"derivedFrom":subQ0}),-1.0]])]});}
            var Q12;
            {var subQ0=sQuery(id+"F0.wireOp",EDGE,"E57");Q12=makeQuery(id+"F0.imprint","IMPRINT",FACE,{"disambiguationData":[TD([[makeQuery(id+"F0.imprint","IMPRINT",EDGE,{"derivedFrom":subQ0}),1.0]])]});}
            var Q13;
            {var subQ0=sQuery(id+"F0.wireOp",EDGE,"E303.MirrorCS");Q13=makeQuery(id+"F0.imprint","IMPRINT",FACE,{"disambiguationData":[TD([[makeQuery(id+"F0.imprint","IMPRINT",EDGE,{"derivedFrom":subQ0}),-1.0]])]});}
            var Q14;
            {var subQ0=sQuery(id+"F0.wireOp",EDGE,"E66");Q14=makeQuery(id+"F0.imprint","IMPRINT",FACE,{"disambiguationData":[TD([[makeQuery(id+"F0.imprint","IMPRINT",EDGE,{"derivedFrom":subQ0}),1.0]])]});}
            var Q15;
            {var subQ0=sQuery(id+"F0.wireOp",EDGE,"E58");Q15=makeQuery(id+"F0.imprint","IMPRINT",FACE,{"disambiguationData":[TD([[makeQuery(id+"F0.imprint","IMPRINT",EDGE,{"derivedFrom":subQ0}),-1.0]])]});}
            var Q16;
            {var subQ0=sQuery(id+"F0.wireOp",EDGE,"E305.MirrorCS");Q16=makeQuery(id+"F0.imprint","IMPRINT",FACE,{"disambiguationData":[TD([[makeQuery(id+"F0.imprint","IMPRINT",EDGE,{"derivedFrom":subQ0}),-1.0]])]});}
            var Q17;
            {var subQ0=sQuery(id+"F0.wireOp",EDGE,"E122");Q17=makeQuery(id+"F0.imprint","IMPRINT",FACE,{"disambiguationData":[TD([[makeQuery(id+"F0.imprint","IMPRINT",EDGE,{"derivedFrom":subQ0}),-1.0]])]});}
            var Q18;
            {var subQ0=sQuery(id+"F0.wireOp",EDGE,"E60");Q18=makeQuery(id+"F0.imprint","IMPRINT",FACE,{"disambiguationData":[TD([[makeQuery(id+"F0.imprint","IMPRINT",EDGE,{"derivedFrom":subQ0}),-1.0]])]});}
            var Q19;
            {var subQ0=sQuery(id+"F0.wireOp",EDGE,"E68");Q19=makeQuery(id+"F0.imprint","IMPRINT",FACE,{"disambiguationData":[TD([[makeQuery(id+"F0.imprint","IMPRINT",EDGE,{"derivedFrom":subQ0}),1.0]])]});}
            var Q20;
            {var subQ0=sQuery(id+"F0.wireOp",EDGE,"E361.MirrorCS");Q20=makeQuery(id+"F0.imprint","IMPRINT",FACE,{"disambiguationData":[TD([[makeQuery(id+"F0.imprint","IMPRINT",EDGE,{"derivedFrom":subQ0}),1.0]])]});}
            var Q21;
            {var subQ0=sQuery(id+"F0.wireOp",EDGE,"E157");Q21=makeQuery(id+"F0.imprint","IMPRINT",FACE,{"disambiguationData":[TD([[makeQuery(id+"F0.imprint","IMPRINT",EDGE,{"derivedFrom":subQ0}),1.0]])]});}
            var Q22;
            {var subQ0=sQuery(id+"F0.wireOp",EDGE,"E258.MirrorCS");Q22=makeQuery(id+"F0.imprint","IMPRINT",FACE,{"disambiguationData":[TD([[makeQuery(id+"F0.imprint","IMPRINT",EDGE,{"derivedFrom":subQ0}),1.0]])]});}
            var Q23;
            {var subQ0=sQuery(id+"F0.wireOp",EDGE,"E123");Q23=makeQuery(id+"F0.imprint","IMPRINT",FACE,{"disambiguationData":[TD([[makeQuery(id+"F0.imprint","IMPRINT",EDGE,{"derivedFrom":subQ0}),1.0]])]});}
            var Q24;
            {var subQ0=sQuery(id+"F0.wireOp",EDGE,"E64");Q24=makeQuery(id+"F0.imprint","IMPRINT",FACE,{"disambiguationData":[TD([[makeQuery(id+"F0.imprint","IMPRINT",EDGE,{"derivedFrom":subQ0}),-1.0]])]});}
            var Q25;
            {var subQ0=sQuery(id+"F0.wireOp",EDGE,"E359.MirrorCS");Q25=makeQuery(id+"F0.imprint","IMPRINT",FACE,{"disambiguationData":[TD([[makeQuery(id+"F0.imprint","IMPRINT",EDGE,{"derivedFrom":subQ0}),1.0]])]});}
            var Q26;
            {var subQ0=sQuery(id+"F0.wireOp",EDGE,"E385.MirrorCS");Q26=makeQuery(id+"F0.imprint","IMPRINT",FACE,{"disambiguationData":[TD([[makeQuery(id+"F0.imprint","IMPRINT",EDGE,{"derivedFrom":subQ0}),1.0]])]});}
            var Q27;
            {var subQ0=sQuery(id+"F0.wireOp",EDGE,"E311.MirrorCS");Q27=makeQuery(id+"F0.imprint","IMPRINT",FACE,{"disambiguationData":[TD([[makeQuery(id+"F0.imprint","IMPRINT",EDGE,{"derivedFrom":subQ0}),1.0]])]});}
            var Q28;
            {var subQ2=sQuery(id+"F0.wireOp",EDGE,"E124");Q28=makeQuery(id+"F0.imprint","IMPRINT",FACE,{"disambiguationData":[TD([[makeQuery(id+"F0.imprint","IMPRINT",EDGE,{"derivedFrom":subQ2}),1.0]])]});}
            var Q29;
            {var subQ0=sQuery(id+"F0.wireOp",EDGE,"E67");Q29=makeQuery(id+"F0.imprint","IMPRINT",FACE,{"disambiguationData":[TD([[makeQuery(id+"F0.imprint","IMPRINT",EDGE,{"derivedFrom":subQ0}),1.0]])]});}
            var Q30;
            {var subQ0=sQuery(id+"F0.wireOp",EDGE,"E54");Q30=makeQuery(id+"F0.imprint","IMPRINT",FACE,{"disambiguationData":[TD([[makeQuery(id+"F0.imprint","IMPRINT",EDGE,{"derivedFrom":subQ0}),-1.0]])]});}
            var Q31;
            {var subQ0=sQuery(id+"F0.wireOp",EDGE,"E360.MirrorCS");Q31=makeQuery(id+"F0.imprint","IMPRINT",FACE,{"disambiguationData":[TD([[makeQuery(id+"F0.imprint","IMPRINT",EDGE,{"derivedFrom":subQ0}),1.0]])]});}
            var Q32;
            {var subQ0=sQuery(id+"F0.wireOp",EDGE,"E394.MirrorCS");Q32=makeQuery(id+"F0.imprint","IMPRINT",FACE,{"disambiguationData":[TD([[makeQuery(id+"F0.imprint","IMPRINT",EDGE,{"derivedFrom":subQ0}),1.0]])]});}
            var Q33;
            {var subQ0=sQuery(id+"F0.wireOp",EDGE,"E265.MirrorCS");Q33=makeQuery(id+"F0.imprint","IMPRINT",FACE,{"disambiguationData":[TD([[makeQuery(id+"F0.imprint","IMPRINT",EDGE,{"derivedFrom":subQ0}),1.0]])]});}
            var Q34;
            {var subQ0=sQuery(id+"F0.wireOp",EDGE,"E11");Q34=makeQuery(id+"F0.imprint","IMPRINT",FACE,{"disambiguationData":[TD([[makeQuery(id+"F0.imprint","IMPRINT",EDGE,{"derivedFrom":subQ0}),-1.0]])]});}
            var Q35;
            {var subQ0=sQuery(id+"F0.wireOp",EDGE,"E382.MirrorCS");Q35=makeQuery(id+"F0.imprint","IMPRINT",FACE,{"disambiguationData":[TD([[makeQuery(id+"F0.imprint","IMPRINT",EDGE,{"derivedFrom":subQ0}),1.0]])]});}
            var Q36;
            Q36=makeQuery(id+"F0.imprint","IMPRINT",FACE,{"disambiguationData":[TD([[makeQuery(id+"F0.imprint","IMPRINT",EDGE,{"derivedFrom":sQuery(id+"F0.wireOp",EDGE,"E241.MirrorCS")}),1.0]])]});
            var Q37;
            {var subQ0=sQuery(id+"F0.wireOp",EDGE,"E386.MirrorCS");Q37=makeQuery(id+"F0.imprint","IMPRINT",FACE,{"disambiguationData":[TD([[makeQuery(id+"F0.imprint","IMPRINT",EDGE,{"derivedFrom":subQ0}),-1.0]])]});}
            var Q38;
            {var subQ0=sQuery(id+"F0.wireOp",EDGE,"E41");Q38=makeQuery(id+"F0.imprint","IMPRINT",FACE,{"disambiguationData":[TD([[makeQuery(id+"F0.imprint","IMPRINT",EDGE,{"derivedFrom":subQ0}),1.0]])]});}
            var Q39;
            {var subQ0=sQuery(id+"F0.wireOp",EDGE,"E271.MirrorCS");Q39=makeQuery(id+"F0.imprint","IMPRINT",FACE,{"disambiguationData":[TD([[makeQuery(id+"F0.imprint","IMPRINT",EDGE,{"derivedFrom":subQ0}),1.0]])]});}
            var Q40;
            {var subQ0=sQuery(id+"F0.wireOp",EDGE,"E43");Q40=makeQuery(id+"F0.imprint","IMPRINT",FACE,{"disambiguationData":[TD([[makeQuery(id+"F0.imprint","IMPRINT",EDGE,{"derivedFrom":subQ0}),1.0]])]});}
            var Q41;
            {var subQ0=sQuery(id+"F0.wireOp",EDGE,"E267.MirrorCS");Q41=makeQuery(id+"F0.imprint","IMPRINT",FACE,{"disambiguationData":[TD([[makeQuery(id+"F0.imprint","IMPRINT",EDGE,{"derivedFrom":subQ0}),-1.0]])]});}
            var Q42;
            {var subQ0=sQuery(id+"F0.wireOp",EDGE,"E276.MirrorCS");Q42=makeQuery(id+"F0.imprint","IMPRINT",FACE,{"disambiguationData":[TD([[makeQuery(id+"F0.imprint","IMPRINT",EDGE,{"derivedFrom":subQ0}),1.0]])]});}
            var Q43;
            Q43=makeQuery(id+"F0.imprint","IMPRINT",FACE,{"disambiguationData":[TD([[makeQuery(id+"F0.imprint","IMPRINT",EDGE,{"derivedFrom":sQuery(id+"F0.wireOp",EDGE,"E0.left")}),1.0]])]});
            var Q44;
            {var subQ0=sQuery(id+"F0.wireOp",EDGE,"E50");Q44=makeQuery(id+"F0.imprint","IMPRINT",FACE,{"disambiguationData":[TD([[makeQuery(id+"F0.imprint","IMPRINT",EDGE,{"derivedFrom":subQ0}),-1.0]])]});}
            var Q45;
            {var subQ0=sQuery(id+"F0.wireOp",EDGE,"E52");Q45=makeQuery(id+"F0.imprint","IMPRINT",FACE,{"disambiguationData":[TD([[makeQuery(id+"F0.imprint","IMPRINT",EDGE,{"derivedFrom":subQ0}),-1.0]])]});}
            var Q46;
            {var subQ0=sQuery(id+"F0.wireOp",EDGE,"E159");Q46=makeQuery(id+"F0.imprint","IMPRINT",FACE,{"disambiguationData":[TD([[makeQuery(id+"F0.imprint","IMPRINT",EDGE,{"derivedFrom":subQ0}),1.0]])]});}
            var Q47;
            {var subQ0=sQuery(id+"F0.wireOp",EDGE,"E45");Q47=makeQuery(id+"F0.imprint","IMPRINT",FACE,{"disambiguationData":[TD([[makeQuery(id+"F0.imprint","IMPRINT",EDGE,{"derivedFrom":subQ0}),1.0]])]});}
            var Q48;
            {var subQ0=sQuery(id+"F0.wireOp",EDGE,"E161");Q48=makeQuery(id+"F0.imprint","IMPRINT",FACE,{"disambiguationData":[TD([[makeQuery(id+"F0.imprint","IMPRINT",EDGE,{"derivedFrom":subQ0}),1.0]])]});}
            var Q49;
            {var subQ0=sQuery(id+"F0.wireOp",EDGE,"E250.MirrorCS");Q49=makeQuery(id+"F0.imprint","IMPRINT",FACE,{"disambiguationData":[TD([[makeQuery(id+"F0.imprint","IMPRINT",EDGE,{"derivedFrom":subQ0}),1.0]])]});}
            var Q50;
            {var subQ0=sQuery(id+"F0.wireOp",EDGE,"E47");Q50=makeQuery(id+"F0.imprint","IMPRINT",FACE,{"disambiguationData":[TD([[makeQuery(id+"F0.imprint","IMPRINT",EDGE,{"derivedFrom":subQ0}),1.0]])]});}
            var Q51;
            {var subQ0=sQuery(id+"F0.wireOp",EDGE,"E49");Q51=makeQuery(id+"F0.imprint","IMPRINT",FACE,{"disambiguationData":[TD([[makeQuery(id+"F0.imprint","IMPRINT",EDGE,{"derivedFrom":subQ0}),1.0]])]});}
            var Q52;
            {var subQ0=sQuery(id+"F0.wireOp",EDGE,"E56");Q52=makeQuery(id+"F0.imprint","IMPRINT",FACE,{"disambiguationData":[TD([[makeQuery(id+"F0.imprint","IMPRINT",EDGE,{"derivedFrom":subQ0}),1.0]])]});}
            var Q53;
            {var subQ0=sQuery(id+"F0.wireOp",EDGE,"E298.MirrorCS");Q53=makeQuery(id+"F0.imprint","IMPRINT",FACE,{"disambiguationData":[TD([[makeQuery(id+"F0.imprint","IMPRINT",EDGE,{"derivedFrom":subQ0}),-1.0]])]});}
            var Q54;
            {var subQ0=sQuery(id+"F0.wireOp",EDGE,"E128");Q54=makeQuery(id+"F0.imprint","IMPRINT",FACE,{"disambiguationData":[TD([[makeQuery(id+"F0.imprint","IMPRINT",EDGE,{"derivedFrom":subQ0}),-1.0]])]});}
            var Q55;
            {var subQ0=sQuery(id+"F0.wireOp",EDGE,"E334.MirrorCS");Q55=makeQuery(id+"F0.imprint","IMPRINT",FACE,{"disambiguationData":[TD([[makeQuery(id+"F0.imprint","IMPRINT",EDGE,{"derivedFrom":subQ0}),1.0]])]});}
            var Q56;
            {var subQ0=sQuery(id+"F0.wireOp",EDGE,"E341.MirrorCS");Q56=makeQuery(id+"F0.imprint","IMPRINT",FACE,{"disambiguationData":[TD([[makeQuery(id+"F0.imprint","IMPRINT",EDGE,{"derivedFrom":subQ0}),-1.0]])]});}
            var Q57;
            {var subQ0=sQuery(id+"F0.wireOp",EDGE,"E44");Q57=makeQuery(id+"F0.imprint","IMPRINT",FACE,{"disambiguationData":[TD([[makeQuery(id+"F0.imprint","IMPRINT",EDGE,{"derivedFrom":subQ0}),1.0]])]});}
            var Q58;
            {var subQ0=sQuery(id+"F0.wireOp",EDGE,"E121");Q58=makeQuery(id+"F0.imprint","IMPRINT",FACE,{"disambiguationData":[TD([[makeQuery(id+"F0.imprint","IMPRINT",EDGE,{"derivedFrom":subQ0}),-1.0]])]});}
            var Q59;
            {var subQ0=sQuery(id+"F0.wireOp",EDGE,"E337.MirrorCS");Q59=makeQuery(id+"F0.imprint","IMPRINT",FACE,{"disambiguationData":[TD([[makeQuery(id+"F0.imprint","IMPRINT",EDGE,{"derivedFrom":subQ0}),1.0]])]});}
            var Q60;
            {var subQ0=sQuery(id+"F0.wireOp",EDGE,"E384.MirrorCS");var subQ1=sQuery(id+"F0.wireOp",EDGE,"E321.MirrorCS");var subQ2=makeQuery(id+"F0.imprint","INTERSECT",VERTEX,{"derivedFrom":[subQ1,subQ0]});Q60=makeQuery(id+"F0.imprint","IMPRINT",FACE,{"disambiguationData":[TD([[makeQuery(id+"F0.imprint","IMPRINT",EDGE,{"disambiguationData":[TD([[subQ2,1.0]])],"derivedFrom":subQ1}),1.0]])]});}
            var Q61;
            {var subQ0=sQuery(id+"F0.wireOp",EDGE,"E99");Q61=makeQuery(id+"F0.imprint","IMPRINT",FACE,{"disambiguationData":[TD([[makeQuery(id+"F0.imprint","IMPRINT",EDGE,{"derivedFrom":subQ0}),1.0]])]});}
            var Q62;
            {var subQ0=sQuery(id+"F0.wireOp",EDGE,"E257.MirrorCS");Q62=makeQuery(id+"F0.imprint","IMPRINT",FACE,{"disambiguationData":[TD([[makeQuery(id+"F0.imprint","IMPRINT",EDGE,{"derivedFrom":subQ0}),1.0]])]});}
            var Q63;
            {var subQ0=sQuery(id+"F0.wireOp",EDGE,"E349.MirrorCS");Q63=makeQuery(id+"F0.imprint","IMPRINT",FACE,{"disambiguationData":[TD([[makeQuery(id+"F0.imprint","IMPRINT",EDGE,{"derivedFrom":subQ0}),1.0]])]});}
            var Q64;
            {var subQ0=sQuery(id+"F0.wireOp",EDGE,"E309.MirrorCS");Q64=makeQuery(id+"F0.imprint","IMPRINT",FACE,{"disambiguationData":[TD([[makeQuery(id+"F0.imprint","IMPRINT",EDGE,{"derivedFrom":subQ0}),1.0]])]});}
            var Q65;
            Q65=makeQuery(id+"F0.imprint","IMPRINT",FACE,{"disambiguationData":[TD([[makeQuery(id+"F0.imprint","IMPRINT",EDGE,{"derivedFrom":sQuery(id+"F0.wireOp",EDGE,"E340.MirrorCS")}),-1.0]])]});
            var Q66;
            {var subQ0=sQuery(id+"F0.wireOp",EDGE,"E115");Q66=makeQuery(id+"F0.imprint","IMPRINT",FACE,{"disambiguationData":[TD([[makeQuery(id+"F0.imprint","IMPRINT",EDGE,{"derivedFrom":subQ0}),-1.0]])]});}
            var Q67;
            {var subQ0=sQuery(id+"F0.wireOp",EDGE,"E30");Q67=makeQuery(id+"F0.imprint","IMPRINT",FACE,{"disambiguationData":[TD([[makeQuery(id+"F0.imprint","IMPRINT",EDGE,{"derivedFrom":subQ0}),1.0]])]});}
            var Q68;
            Q68=makeQuery(id+"F0.imprint","IMPRINT",FACE,{"disambiguationData":[TD([[makeQuery(id+"F0.imprint","IMPRINT",EDGE,{"derivedFrom":sQuery(id+"F0.wireOp",EDGE,"E312.MirrorCS")}),1.0]])]});
            var Q69;
            {var subQ0=sQuery(id+"F0.wireOp",EDGE,"E261.MirrorCS");Q69=makeQuery(id+"F0.imprint","IMPRINT",FACE,{"disambiguationData":[TD([[makeQuery(id+"F0.imprint","IMPRINT",EDGE,{"derivedFrom":subQ0}),-1.0]])]});}
            var Q70;
            {var subQ0=sQuery(id+"F0.wireOp",EDGE,"E132");Q70=makeQuery(id+"F0.imprint","IMPRINT",FACE,{"disambiguationData":[TD([[makeQuery(id+"F0.imprint","IMPRINT",EDGE,{"derivedFrom":subQ0}),1.0]])]});}
            var Q71;
            {var subQ5=sQuery(id+"F0.wireOp",EDGE,"E167");Q71=makeQuery(id+"F0.imprint","IMPRINT",FACE,{"disambiguationData":[TD([[makeQuery(id+"F0.imprint","IMPRINT",EDGE,{"derivedFrom":subQ5}),1.0]])]});}
            var Q72;
            Q72=makeQuery(id+"F0.imprint","IMPRINT",FACE,{"disambiguationData":[TD([[makeQuery(id+"F0.imprint","IMPRINT",EDGE,{"derivedFrom":sQuery(id+"F0.wireOp",EDGE,"E310.MirrorCS")}),-1.0]])]});
            var Q73;
            {var subQ4=sQuery(id+"F0.wireOp",EDGE,"E404.MirrorCS");Q73=makeQuery(id+"F0.imprint","IMPRINT",FACE,{"disambiguationData":[TD([[makeQuery(id+"F0.imprint","IMPRINT",EDGE,{"derivedFrom":subQ4}),-1.0]])]});}
            var Q74;
            {var subQ0=sQuery(id+"F0.wireOp",EDGE,"E115");Q74=makeQuery(id+"F0.imprint","IMPRINT",FACE,{"disambiguationData":[TD([[makeQuery(id+"F0.imprint","IMPRINT",EDGE,{"derivedFrom":subQ0}),1.0]])]});}
            var Q75;
            Q75=makeQuery(id+"F0.imprint","IMPRINT",FACE,{"disambiguationData":[TD([[makeQuery(id+"F0.imprint","IMPRINT",EDGE,{"derivedFrom":sQuery(id+"F0.wireOp",EDGE,"E28")}),-1.0]])]});
            var Q76;
            {var subQ0=sQuery(id+"F0.wireOp",EDGE,"E314.MirrorCS");Q76=makeQuery(id+"F0.imprint","IMPRINT",FACE,{"disambiguationData":[TD([[makeQuery(id+"F0.imprint","IMPRINT",EDGE,{"derivedFrom":subQ0}),-1.0]])]});}
            var Q77;
            Q77=makeQuery(id+"F0.imprint","IMPRINT",FACE,{"disambiguationData":[TD([[makeQuery(id+"F0.imprint","IMPRINT",EDGE,{"derivedFrom":sQuery(id+"F0.wireOp",EDGE,"E263.MirrorCS")}),-1.0]])]});
            var Q78;
            {var subQ0=sQuery(id+"F0.wireOp",EDGE,"E134");Q78=makeQuery(id+"F0.imprint","IMPRINT",FACE,{"disambiguationData":[TD([[makeQuery(id+"F0.imprint","IMPRINT",EDGE,{"derivedFrom":subQ0}),-1.0]])]});}
            var Q79;
            {var subQ5=sQuery(id+"F0.wireOp",EDGE,"E430.MirrorCS");Q79=makeQuery(id+"F0.imprint","IMPRINT",FACE,{"disambiguationData":[TD([[makeQuery(id+"F0.imprint","IMPRINT",EDGE,{"derivedFrom":subQ5}),-1.0]])]});}
            var Q80;
            {var subQ1=sQuery(id+"F0.wireOp",EDGE,"E25");Q80=makeQuery(id+"F0.imprint","IMPRINT",FACE,{"disambiguationData":[TD([[makeQuery(id+"F0.imprint","IMPRINT",EDGE,{"derivedFrom":subQ1}),1.0]])]});}
            var Q81;
            {var subQ0=sQuery(id+"F0.wireOp",EDGE,"E365.MirrorCS");Q81=makeQuery(id+"F0.imprint","IMPRINT",FACE,{"disambiguationData":[TD([[makeQuery(id+"F0.imprint","IMPRINT",EDGE,{"derivedFrom":subQ0}),1.0]])]});}
            var Q82;
            {var subQ0=sQuery(id+"F0.wireOp",EDGE,"E36");Q82=makeQuery(id+"F0.imprint","IMPRINT",FACE,{"disambiguationData":[TD([[makeQuery(id+"F0.imprint","IMPRINT",EDGE,{"derivedFrom":subQ0}),1.0]])]});}
            var Q83;
            {var subQ0=sQuery(id+"F0.wireOp",EDGE,"E315.MirrorCS");Q83=makeQuery(id+"F0.imprint","IMPRINT",FACE,{"disambiguationData":[TD([[makeQuery(id+"F0.imprint","IMPRINT",EDGE,{"derivedFrom":subQ0}),-1.0]])]});}
            var Q84;
            {var subQ0=sQuery(id+"F0.wireOp",EDGE,"E164");Q84=makeQuery(id+"F0.imprint","IMPRINT",FACE,{"disambiguationData":[TD([[makeQuery(id+"F0.imprint","IMPRINT",EDGE,{"derivedFrom":subQ0}),1.0]])]});}
            var Q85;
            {var subQ5=sQuery(id+"F0.wireOp",EDGE,"E450.MirrorCS");Q85=makeQuery(id+"F0.imprint","IMPRINT",FACE,{"disambiguationData":[TD([[makeQuery(id+"F0.imprint","IMPRINT",EDGE,{"derivedFrom":subQ5}),-1.0]])]});}
            var Q86;
            {var subQ0=sQuery(id+"F0.wireOp",EDGE,"E38");Q86=makeQuery(id+"F0.imprint","IMPRINT",FACE,{"disambiguationData":[TD([[makeQuery(id+"F0.imprint","IMPRINT",EDGE,{"derivedFrom":subQ0}),1.0]])]});}
            var Q87;
            {var subQ1=sQuery(id+"F0.wireOp",EDGE,"E316.MirrorCS");Q87=makeQuery(id+"F0.imprint","IMPRINT",FACE,{"disambiguationData":[TD([[makeQuery(id+"F0.imprint","IMPRINT",EDGE,{"derivedFrom":subQ1}),-1.0]])]});}
            var Q88;
            {var subQ0=sQuery(id+"F0.wireOp",EDGE,"E266.MirrorCS");Q88=makeQuery(id+"F0.imprint","IMPRINT",FACE,{"disambiguationData":[TD([[makeQuery(id+"F0.imprint","IMPRINT",EDGE,{"derivedFrom":subQ0}),-1.0]])]});}
            var Q89;
            {var subQ0=sQuery(id+"F0.wireOp",EDGE,"E72");Q89=makeQuery(id+"F0.imprint","IMPRINT",FACE,{"disambiguationData":[TD([[makeQuery(id+"F0.imprint","IMPRINT",EDGE,{"derivedFrom":subQ0}),-1.0]])]});}
            var Q90;
            {var subQ0=sQuery(id+"F0.wireOp",EDGE,"E244.MirrorCS");Q90=makeQuery(id+"F0.imprint","IMPRINT",FACE,{"disambiguationData":[TD([[makeQuery(id+"F0.imprint","IMPRINT",EDGE,{"derivedFrom":subQ0}),-1.0]])]});}
            var Q91;
            {var subQ0=sQuery(id+"F0.wireOp",EDGE,"E39");Q91=makeQuery(id+"F0.imprint","IMPRINT",FACE,{"disambiguationData":[TD([[makeQuery(id+"F0.imprint","IMPRINT",EDGE,{"derivedFrom":subQ0}),-1.0]])]});}
            var Q92;
            {var subQ0=sQuery(id+"F0.wireOp",EDGE,"E318.MirrorCS");Q92=makeQuery(id+"F0.imprint","IMPRINT",FACE,{"disambiguationData":[TD([[makeQuery(id+"F0.imprint","IMPRINT",EDGE,{"derivedFrom":subQ0}),1.0]])]});}
            var Q93;
            {var subQ0=sQuery(id+"F0.wireOp",EDGE,"E270.MirrorCS");Q93=makeQuery(id+"F0.imprint","IMPRINT",FACE,{"disambiguationData":[TD([[makeQuery(id+"F0.imprint","IMPRINT",EDGE,{"derivedFrom":subQ0}),1.0]])]});}
            var Q94;
            {var subQ0=sQuery(id+"F0.wireOp",EDGE,"E73");Q94=makeQuery(id+"F0.imprint","IMPRINT",FACE,{"disambiguationData":[TD([[makeQuery(id+"F0.imprint","IMPRINT",EDGE,{"derivedFrom":subQ0}),-1.0]])]});}
            var Q95;
            {var subQ0=sQuery(id+"F0.wireOp",EDGE,"E260.MirrorCS");Q95=makeQuery(id+"F0.imprint","IMPRINT",FACE,{"disambiguationData":[TD([[makeQuery(id+"F0.imprint","IMPRINT",EDGE,{"derivedFrom":subQ0}),1.0]])]});}
            var Q96;
            Q96=makeQuery(id+"F0.imprint","IMPRINT",FACE,{"disambiguationData":[TD([[makeQuery(id+"F0.imprint","IMPRINT",EDGE,{"derivedFrom":sQuery(id+"F0.wireOp",EDGE,"E29")}),1.0]])]});
            var Q97;
            {var subQ0=sQuery(id+"F0.wireOp",EDGE,"E237.trimOffspring");var subQ1=sQuery(id+"F0.wireOp",EDGE,"E2");var subQ2=makeQuery(id+"F0.imprint","INTERSECT",VERTEX,{"derivedFrom":[subQ1,subQ0]});Q97=makeQuery(id+"F0.imprint","IMPRINT",FACE,{"disambiguationData":[TD([[makeQuery(id+"F0.imprint","IMPRINT",EDGE,{"disambiguationData":[TD([[subQ2,-1.0]])],"derivedFrom":subQ1}),-1.0]])]});}
            var Q98;
            Q98=makeQuery(id+"F0.imprint","IMPRINT",FACE,{"disambiguationData":[TD([[makeQuery(id+"F0.imprint","IMPRINT",EDGE,{"derivedFrom":sQuery(id+"F0.wireOp",EDGE,"E388.MirrorCS")}),-1.0]])]});
            var Q99;
            Q99=makeQuery(id+"F0.imprint","IMPRINT",FACE,{"disambiguationData":[TD([[makeQuery(id+"F0.imprint","IMPRINT",EDGE,{"derivedFrom":sQuery(id+"F0.wireOp",EDGE,"E319.MirrorCS")}),-1.0]])]});
            var Q100;
            {var subQ0=sQuery(id+"F0.wireOp",EDGE,"E246.MirrorCS");Q100=makeQuery(id+"F0.imprint","IMPRINT",FACE,{"disambiguationData":[TD([[makeQuery(id+"F0.imprint","IMPRINT",EDGE,{"derivedFrom":subQ0}),1.0]])]});}
            var Q101;
            {var subQ0=sQuery(id+"F0.wireOp",EDGE,"E260.MirrorCS");Q101=makeQuery(id+"F0.imprint","IMPRINT",FACE,{"disambiguationData":[TD([[makeQuery(id+"F0.imprint","IMPRINT",EDGE,{"derivedFrom":subQ0}),-1.0]])]});}
            var Q102;
            {var subQ0=sQuery(id+"F0.wireOp",EDGE,"E40");Q102=makeQuery(id+"F0.imprint","IMPRINT",FACE,{"disambiguationData":[TD([[makeQuery(id+"F0.imprint","IMPRINT",EDGE,{"derivedFrom":subQ0}),1.0]])]});}
            var Q103;
            {var subQ0=sQuery(id+"F0.wireOp",EDGE,"E128");Q103=makeQuery(id+"F0.imprint","IMPRINT",FACE,{"disambiguationData":[TD([[makeQuery(id+"F0.imprint","IMPRINT",EDGE,{"derivedFrom":subQ0}),1.0]])]});}
            var Q104;
            {var subQ0=sQuery(id+"F0.wireOp",EDGE,"E390.MirrorCS");Q104=makeQuery(id+"F0.imprint","IMPRINT",FACE,{"disambiguationData":[TD([[makeQuery(id+"F0.imprint","IMPRINT",EDGE,{"derivedFrom":subQ0}),1.0]])]});}
            var Q105;
            {var subQ0=sQuery(id+"F0.wireOp",EDGE,"E320.MirrorCS");Q105=makeQuery(id+"F0.imprint","IMPRINT",FACE,{"disambiguationData":[TD([[makeQuery(id+"F0.imprint","IMPRINT",EDGE,{"derivedFrom":subQ0}),-1.0]])]});}
            var Q106;
            {var subQ0=sQuery(id+"F0.wireOp",EDGE,"E275.MirrorCS");Q106=makeQuery(id+"F0.imprint","IMPRINT",FACE,{"disambiguationData":[TD([[makeQuery(id+"F0.imprint","IMPRINT",EDGE,{"derivedFrom":subQ0}),-1.0]])]});}
            var Q107;
            {var subQ4=sQuery(id+"F0.wireOp",EDGE,"E249.MirrorCS");Q107=makeQuery(id+"F0.imprint","IMPRINT",FACE,{"disambiguationData":[TD([[makeQuery(id+"F0.imprint","IMPRINT",EDGE,{"derivedFrom":subQ4}),1.0]])]});}
            var Q108;
            {var subQ0=sQuery(id+"F0.wireOp",EDGE,"E100");Q108=makeQuery(id+"F0.imprint","IMPRINT",FACE,{"disambiguationData":[TD([[makeQuery(id+"F0.imprint","IMPRINT",EDGE,{"derivedFrom":subQ0}),1.0]])]});}
            var Q109;
            {var subQ0=sQuery(id+"F0.wireOp",EDGE,"E119");Q109=makeQuery(id+"F0.imprint","IMPRINT",FACE,{"disambiguationData":[TD([[makeQuery(id+"F0.imprint","IMPRINT",EDGE,{"derivedFrom":subQ0}),-1.0]])]});}
            var Q110;
            {var subQ0=sQuery(id+"F0.wireOp",EDGE,"E396.MirrorCS");Q110=makeQuery(id+"F0.imprint","IMPRINT",FACE,{"disambiguationData":[TD([[makeQuery(id+"F0.imprint","IMPRINT",EDGE,{"derivedFrom":subQ0}),-1.0]])]});}
            var Q111;
            {var subQ0=sQuery(id+"F0.wireOp",EDGE,"E116");Q111=makeQuery(id+"F0.imprint","IMPRINT",FACE,{"disambiguationData":[TD([[makeQuery(id+"F0.imprint","IMPRINT",EDGE,{"derivedFrom":subQ0}),1.0]])]});}
            var Q112;
            {var subQ0=sQuery(id+"F0.wireOp",EDGE,"E398.MirrorCS");Q112=makeQuery(id+"F0.imprint","IMPRINT",FACE,{"disambiguationData":[TD([[makeQuery(id+"F0.imprint","IMPRINT",EDGE,{"derivedFrom":subQ0}),-1.0]])]});}
            var Q113;
            {var subQ0=sQuery(id+"F0.wireOp",EDGE,"E324.MirrorCS");Q113=makeQuery(id+"F0.imprint","IMPRINT",FACE,{"disambiguationData":[TD([[makeQuery(id+"F0.imprint","IMPRINT",EDGE,{"derivedFrom":subQ0}),-1.0]])]});}
            var Q114;
            {var subQ0=sQuery(id+"F0.wireOp",EDGE,"E277.MirrorCS");Q114=makeQuery(id+"F0.imprint","IMPRINT",FACE,{"disambiguationData":[TD([[makeQuery(id+"F0.imprint","IMPRINT",EDGE,{"derivedFrom":subQ0}),1.0]])]});}
            var Q115;
            {var subQ0=sQuery(id+"F0.wireOp",EDGE,"E248.MirrorCS");Q115=makeQuery(id+"F0.imprint","IMPRINT",FACE,{"disambiguationData":[TD([[makeQuery(id+"F0.imprint","IMPRINT",EDGE,{"derivedFrom":subQ0}),-1.0]])]});}
            var Q116;
            Q116=makeQuery(id+"F0.imprint","IMPRINT",FACE,{"disambiguationData":[TD([[makeQuery(id+"F0.imprint","IMPRINT",EDGE,{"derivedFrom":sQuery(id+"F0.wireOp",EDGE,"E27")}),-1.0]])]});
            var Q117;
            {var subQ2=sQuery(id+"F0.wireOp",EDGE,"E32");Q117=makeQuery(id+"F0.imprint","IMPRINT",FACE,{"disambiguationData":[TD([[makeQuery(id+"F0.imprint","IMPRINT",EDGE,{"derivedFrom":subQ2}),1.0]])]});}
            var Q118;
            {var subQ0=sQuery(id+"F0.wireOp",EDGE,"E24");Q118=makeQuery(id+"F0.imprint","IMPRINT",FACE,{"disambiguationData":[TD([[makeQuery(id+"F0.imprint","IMPRINT",EDGE,{"derivedFrom":subQ0}),-1.0]])]});}
            var Q119;
            Q119=makeQuery(id+"F0.imprint","IMPRINT",FACE,{"disambiguationData":[TD([[makeQuery(id+"F0.imprint","IMPRINT",EDGE,{"derivedFrom":sQuery(id+"F0.wireOp",EDGE,"E0.bottom")}),-1.0]])]});
            var Q120;
            Q120=makeQuery(id+"F0.imprint","IMPRINT",FACE,{"disambiguationData":[TD([[makeQuery(id+"F0.imprint","IMPRINT",EDGE,{"derivedFrom":sQuery(id+"F0.wireOp",EDGE,"E8.top")}),-1.0]])]});
            var Q121;
            {var subQ0=sQuery(id+"F0.wireOp",EDGE,"E101");Q121=makeQuery(id+"F0.imprint","IMPRINT",FACE,{"disambiguationData":[TD([[makeQuery(id+"F0.imprint","IMPRINT",EDGE,{"derivedFrom":subQ0}),-1.0]])]});}
            var Q122;
            {var subQ0=sQuery(id+"F0.wireOp",EDGE,"E23");Q122=makeQuery(id+"F0.imprint","IMPRINT",FACE,{"disambiguationData":[TD([[makeQuery(id+"F0.imprint","IMPRINT",EDGE,{"derivedFrom":subQ0}),1.0]])]});}
            var Q123;
            {var subQ0=sQuery(id+"F0.wireOp",EDGE,"E145");Q123=makeQuery(id+"F0.imprint","IMPRINT",FACE,{"disambiguationData":[TD([[makeQuery(id+"F0.imprint","IMPRINT",EDGE,{"derivedFrom":subQ0}),-1.0]])]});}
            var Q124;
            {var subQ0=sQuery(id+"F0.wireOp",EDGE,"E33");Q124=makeQuery(id+"F0.imprint","IMPRINT",FACE,{"disambiguationData":[TD([[makeQuery(id+"F0.imprint","IMPRINT",EDGE,{"derivedFrom":subQ0}),-1.0]])]});}
            var Q125;
            {var subQ0=sQuery(id+"F0.wireOp",EDGE,"E42");Q125=makeQuery(id+"F0.imprint","IMPRINT",FACE,{"disambiguationData":[TD([[makeQuery(id+"F0.imprint","IMPRINT",EDGE,{"derivedFrom":subQ0}),1.0]])]});}
            var Q126;
            {var subQ0=sQuery(id+"F0.wireOp",EDGE,"E34");Q126=makeQuery(id+"F0.imprint","IMPRINT",FACE,{"disambiguationData":[TD([[makeQuery(id+"F0.imprint","IMPRINT",EDGE,{"derivedFrom":subQ0}),1.0]])]});}
            var Q127;
            {var subQ0=sQuery(id+"F0.wireOp",EDGE,"E103");Q127=makeQuery(id+"F0.imprint","IMPRINT",FACE,{"disambiguationData":[TD([[makeQuery(id+"F0.imprint","IMPRINT",EDGE,{"derivedFrom":subQ0}),1.0]])]});}
            var Q128;
            {var subQ0=sQuery(id+"F0.wireOp",EDGE,"E406.MirrorCS");Q128=makeQuery(id+"F0.imprint","IMPRINT",FACE,{"disambiguationData":[TD([[makeQuery(id+"F0.imprint","IMPRINT",EDGE,{"derivedFrom":subQ0}),-1.0]])]});}
            var Q129;
            Q129=makeQuery(id+"F0.imprint","IMPRINT",FACE,{"disambiguationData":[TD([[makeQuery(id+"F0.imprint","IMPRINT",EDGE,{"derivedFrom":sQuery(id+"F0.wireOp",EDGE,"E279.MirrorCS")}),-1.0]])]});
            var Q130;
            {var subQ0=sQuery(id+"F0.wireOp",EDGE,"E102");Q130=makeQuery(id+"F0.imprint","IMPRINT",FACE,{"disambiguationData":[TD([[makeQuery(id+"F0.imprint","IMPRINT",EDGE,{"derivedFrom":subQ0}),-1.0]])]});}
            var Q131;
            Q131=makeQuery(id+"F0.imprint","IMPRINT",FACE,{"disambiguationData":[TD([[makeQuery(id+"F0.imprint","IMPRINT",EDGE,{"derivedFrom":sQuery(id+"F0.wireOp",EDGE,"E434.MirrorCS")}),-1.0]])]});
            var Q132;
            Q132=makeQuery(id+"F0.imprint","IMPRINT",FACE,{"disambiguationData":[TD([[makeQuery(id+"F0.imprint","IMPRINT",EDGE,{"derivedFrom":sQuery(id+"F0.wireOp",EDGE,"E328.MirrorCS")}),1.0]])]});
            var Q133;
            {var subQ0=sQuery(id+"F0.wireOp",EDGE,"E299.MirrorCS");Q133=makeQuery(id+"F0.imprint","IMPRINT",FACE,{"disambiguationData":[TD([[makeQuery(id+"F0.imprint","IMPRINT",EDGE,{"derivedFrom":subQ0}),-1.0]])]});}
            var Q134;
            {var subQ0=sQuery(id+"F0.wireOp",EDGE,"E295.MirrorCS");Q134=makeQuery(id+"F0.imprint","IMPRINT",FACE,{"disambiguationData":[TD([[makeQuery(id+"F0.imprint","IMPRINT",EDGE,{"derivedFrom":subQ0}),1.0]])]});}
            var Q135;
            {var subQ0=sQuery(id+"F0.wireOp",EDGE,"E35");Q135=makeQuery(id+"F0.imprint","IMPRINT",FACE,{"disambiguationData":[TD([[makeQuery(id+"F0.imprint","IMPRINT",EDGE,{"derivedFrom":subQ0}),-1.0]])]});}
            var Q136;
            {var subQ0=sQuery(id+"F0.wireOp",EDGE,"E107");Q136=makeQuery(id+"F0.imprint","IMPRINT",FACE,{"disambiguationData":[TD([[makeQuery(id+"F0.imprint","IMPRINT",EDGE,{"derivedFrom":subQ0}),-1.0]])]});}
            var Q137;
            {var subQ0=sQuery(id+"F0.wireOp",EDGE,"E446.MirrorCS");Q137=makeQuery(id+"F0.imprint","IMPRINT",FACE,{"disambiguationData":[TD([[makeQuery(id+"F0.imprint","IMPRINT",EDGE,{"derivedFrom":subQ0}),-1.0]])]});}
            var Q138;
            Q138=makeQuery(id+"F0.imprint","IMPRINT",FACE,{"disambiguationData":[TD([[makeQuery(id+"F0.imprint","IMPRINT",EDGE,{"derivedFrom":sQuery(id+"F0.wireOp",EDGE,"E330.MirrorCS")}),-1.0]])]});
            var Q139;
            {var subQ0=sQuery(id+"F0.wireOp",EDGE,"E249.MirrorCS");Q139=makeQuery(id+"F0.imprint","IMPRINT",FACE,{"disambiguationData":[TD([[makeQuery(id+"F0.imprint","IMPRINT",EDGE,{"derivedFrom":subQ0}),-1.0]])]});}
            var Q140;
            {var subQ5=sQuery(id+"F0.wireOp",EDGE,"E17");Q140=makeQuery(id+"F0.imprint","IMPRINT",FACE,{"disambiguationData":[TD([[makeQuery(id+"F0.imprint","IMPRINT",EDGE,{"derivedFrom":subQ5}),-1.0]])]});}
            var Q141;
            {var subQ0=sQuery(id+"F0.wireOp",EDGE,"E256.MirrorCS");Q141=makeQuery(id+"F0.imprint","IMPRINT",FACE,{"disambiguationData":[TD([[makeQuery(id+"F0.imprint","IMPRINT",EDGE,{"derivedFrom":subQ0}),1.0]])]});}
            var Q142;
            {var subQ4=sQuery(id+"F0.wireOp",EDGE,"E79");Q142=makeQuery(id+"F0.imprint","IMPRINT",FACE,{"disambiguationData":[TD([[makeQuery(id+"F0.imprint","IMPRINT",EDGE,{"derivedFrom":subQ4}),-1.0]])]});}
            var Q143;
            {var subQ0=sQuery(id+"F0.wireOp",EDGE,"E7.bottom");Q143=makeQuery(id+"F0.imprint","IMPRINT",FACE,{"disambiguationData":[TD([[makeQuery(id+"F0.imprint","IMPRINT",EDGE,{"derivedFrom":subQ0}),1.0]])]});}
            var Q144;
            {var subQ4=sQuery(id+"F0.wireOp",EDGE,"E149");Q144=makeQuery(id+"F0.imprint","IMPRINT",FACE,{"disambiguationData":[TD([[makeQuery(id+"F0.imprint","IMPRINT",EDGE,{"derivedFrom":subQ4}),-1.0]])]});}
            var Q145;
            Q145=makeQuery(id+"F0.imprint","IMPRINT",FACE,{"disambiguationData":[TD([[makeQuery(id+"F0.imprint","IMPRINT",EDGE,{"derivedFrom":sQuery(id+"F0.wireOp",EDGE,"E259.MirrorCS")}),1.0]])]});
            var Q146;
            Q146=makeQuery(id+"F0.imprint","IMPRINT",FACE,{"disambiguationData":[TD([[makeQuery(id+"F0.imprint","IMPRINT",EDGE,{"derivedFrom":sQuery(id+"F0.wireOp",EDGE,"E70")}),1.0]])]});
            var Q147;
            Q147=makeQuery(id+"F0.imprint","IMPRINT",FACE,{"disambiguationData":[TD([[makeQuery(id+"F0.imprint","IMPRINT",EDGE,{"derivedFrom":sQuery(id+"F0.wireOp",EDGE,"E71")}),1.0]])]});
            var Q148;
            {var subQ0=sQuery(id+"F0.wireOp",EDGE,"E11");Q148=makeQuery(id+"F0.imprint","IMPRINT",FACE,{"disambiguationData":[TD([[makeQuery(id+"F0.imprint","IMPRINT",EDGE,{"derivedFrom":subQ0}),1.0]])]});}
            var Q149;
            Q149=makeQuery(id+"F0.imprint","IMPRINT",FACE,{"disambiguationData":[TD([[makeQuery(id+"F0.imprint","IMPRINT",EDGE,{"derivedFrom":sQuery(id+"F0.wireOp",EDGE,"E245.MirrorCS")}),-1.0]])]});
            var Q150;
            Q150=makeQuery(id+"F0.imprint","IMPRINT",FACE,{"disambiguationData":[TD([[makeQuery(id+"F0.imprint","IMPRINT",EDGE,{"derivedFrom":sQuery(id+"F0.wireOp",EDGE,"E77")}),-1.0]])]});
            var Q151;
            {var subQ0=sQuery(id+"F0.wireOp",EDGE,"E198");Q151=makeQuery(id+"F0.imprint","IMPRINT",FACE,{"disambiguationData":[TD([[makeQuery(id+"F0.imprint","IMPRINT",EDGE,{"derivedFrom":subQ0}),-1.0]])]});}
            var Q152;
            {var subQ0=sQuery(id+"F0.wireOp",EDGE,"E17");Q152=makeQuery(id+"F0.imprint","IMPRINT",FACE,{"disambiguationData":[TD([[makeQuery(id+"F0.imprint","IMPRINT",EDGE,{"derivedFrom":subQ0}),1.0]])]});}
            var Q153;
            {var subQ0=sQuery(id+"F0.wireOp",EDGE,"E281.MirrorCS");Q153=makeQuery(id+"F0.imprint","IMPRINT",FACE,{"disambiguationData":[TD([[makeQuery(id+"F0.imprint","IMPRINT",EDGE,{"derivedFrom":subQ0}),1.0]])]});}
            var Q154;
            Q154=makeQuery(id+"F0.imprint","IMPRINT",FACE,{"disambiguationData":[TD([[makeQuery(id+"F0.imprint","IMPRINT",EDGE,{"derivedFrom":sQuery(id+"F0.wireOp",EDGE,"E327.MirrorCS")}),-1.0]])]});
            var Q155;
            Q155=makeQuery(id+"F0.imprint","IMPRINT",FACE,{"disambiguationData":[TD([[makeQuery(id+"F0.imprint","IMPRINT",EDGE,{"derivedFrom":sQuery(id+"F0.wireOp",EDGE,"E251.MirrorCS")}),1.0]])]});
            var Q156;
            Q156=makeQuery(id+"F0.imprint","IMPRINT",FACE,{"disambiguationData":[TD([[makeQuery(id+"F0.imprint","IMPRINT",EDGE,{"derivedFrom":sQuery(id+"F0.wireOp",EDGE,"E105")}),-1.0]])]});
            var Q157;
            Q157=makeQuery(id+"F0.imprint","IMPRINT",FACE,{"disambiguationData":[TD([[makeQuery(id+"F0.imprint","IMPRINT",EDGE,{"derivedFrom":sQuery(id+"F0.wireOp",EDGE,"E254.MirrorCS")}),-1.0]])]});
            var Q158;
            {var subQ2=sQuery(id+"F0.wireOp",EDGE,"E16");Q158=makeQuery(id+"F0.imprint","IMPRINT",FACE,{"disambiguationData":[TD([[makeQuery(id+"F0.imprint","IMPRINT",EDGE,{"derivedFrom":subQ2}),-1.0]])]});}
            var Q159;
            {var subQ0=sQuery(id+"F0.wireOp",EDGE,"E502.trimOffspring");Q159=makeQuery(id+"F0.imprint","IMPRINT",FACE,{"disambiguationData":[TD([[makeQuery(id+"F0.imprint","IMPRINT",EDGE,{"derivedFrom":subQ0}),-1.0]])]});}
            var Q160;
            {var subQ5=sQuery(id+"F0.wireOp",EDGE,"E16");Q160=makeQuery(id+"F0.imprint","IMPRINT",FACE,{"disambiguationData":[TD([[makeQuery(id+"F0.imprint","IMPRINT",EDGE,{"derivedFrom":subQ5}),1.0]])]});}
            extrude(context, id + "F1", {"entities" : qUnion([Q0, Q1, Q2, Q3, Q4, Q5, Q6, Q7, Q8, Q9, Q10, Q11, Q12, Q13, Q14, Q15, Q16, Q17, Q18, Q19, Q20, Q21, Q22, Q23, Q24, Q25, Q26, Q27, Q28, Q29, Q30, Q31, Q32, Q33, Q34, Q35, Q36, Q37, Q38, Q39, Q40, Q41, Q42, Q43, Q44, Q45, Q46, Q47, Q48, Q49, Q50, Q51, Q52, Q53, Q54, Q55, Q56, Q57, Q58, Q59, Q60, Q61, Q62, Q63, Q64, Q65, Q66, Q67, Q68, Q69, Q70, Q71, Q72, Q73, Q74, Q75, Q76, Q77, Q78, Q79, Q80, Q81, Q82, Q83, Q84, Q85, Q86, Q87, Q88, Q89, Q90, Q91, Q92, Q93, Q94, Q95, Q96, Q97, Q98, Q99, Q100, Q101, Q102, Q103, Q104, Q105, Q106, Q107, Q108, Q109, Q110, Q111, Q112, Q113, Q114, Q115, Q116, Q117, Q118, Q119, Q120, Q121, Q122, Q123, Q124, Q125, Q126, Q127, Q128, Q129, Q130, Q131, Q132, Q133, Q134, Q135, Q136, Q137, Q138, Q139, Q140, Q141, Q142, Q143, Q144, Q145, Q146, Q147, Q148, Q149, Q150, Q151, Q152, Q153, Q154, Q155, Q156, Q157, Q158, Q159, Q160]), "depth" : 25.4 * mm});
        }
    });
